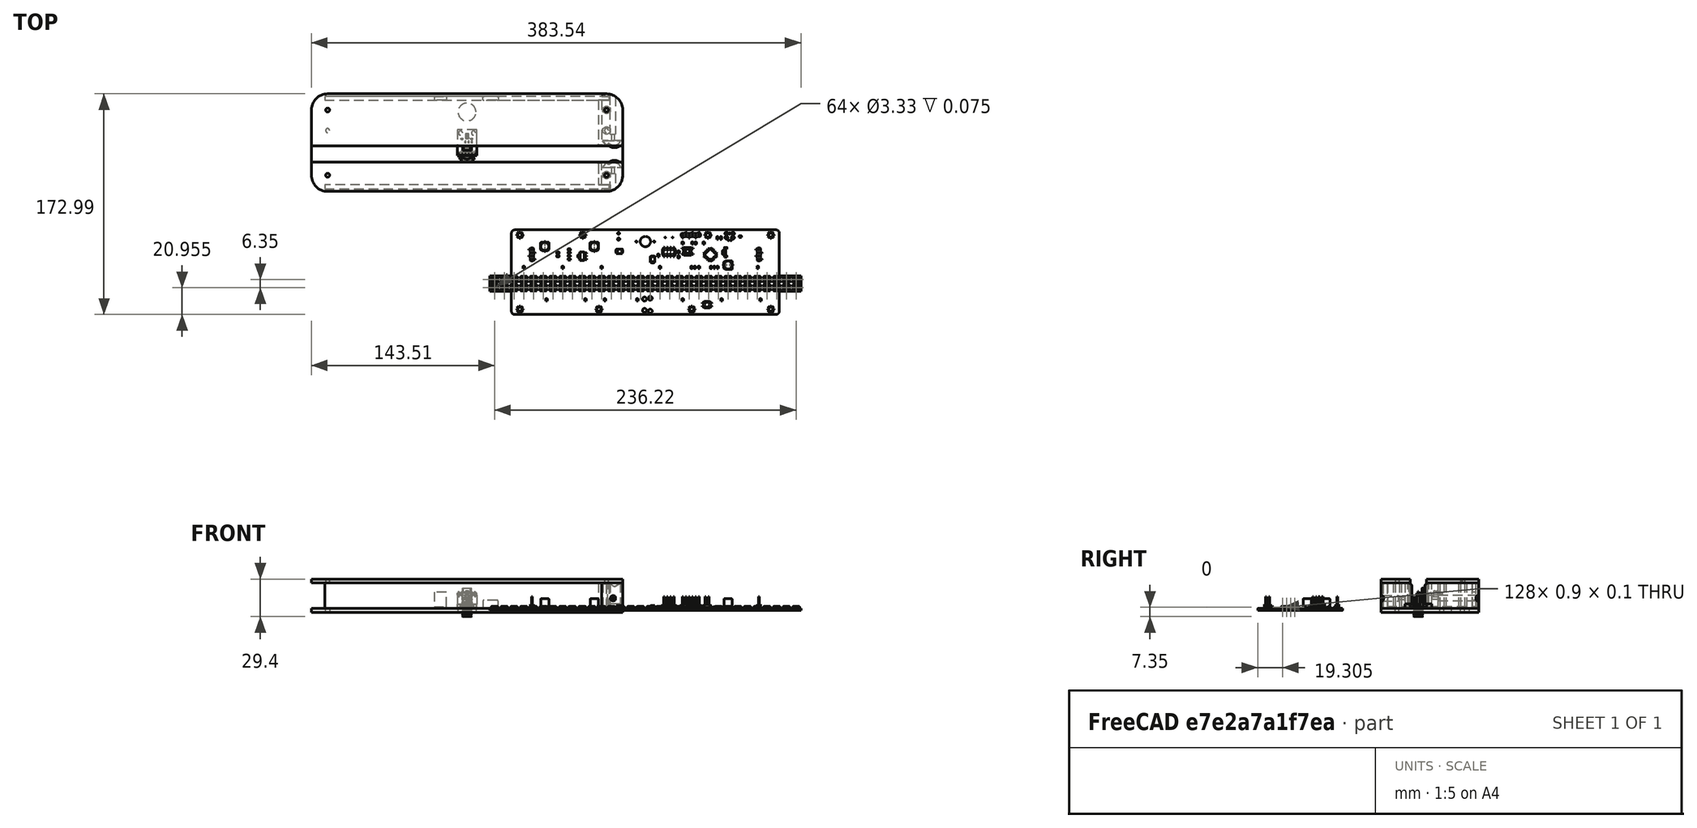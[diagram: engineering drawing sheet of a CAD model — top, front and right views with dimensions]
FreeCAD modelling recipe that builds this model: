
FCSTD DOCUMENT  (FreeCAD 0.21R33675 (Git))
Label: mockup_v2
License: All rights reserved
LicenseURL: http://en.wikipedia.org/wiki/All_rights_reserved
objects: Part::Feature×143, Sketcher::SketchObject×30, PartDesign::Pocket×15, PartDesign::Pad×13, PartDesign::Body×9, App::Part×8, PartDesign::SubShapeBinder×7, Part::Part2DObjectPython×6, PartDesign::ShapeBinder×3, PartDesign::Plane×3, TechDraw::DrawViewDimension×3, Part::Mirroring×2, PartDesign::CoordinateSystem×1, PartDesign::Mirrored×1, Part::FeaturePython×1, TechDraw::DrawSVGTemplate×1, TechDraw::DrawViewPart×1, TechDraw::DrawHatch×1, TechDraw::DrawPage×1
note: 262 computed .brp shape members not serialized (recipe doc carries the construction recipe); baked Part::Feature solids carry a one-line shape summary decoded from their .brp

FEATURE [Sketcher::SketchObject] Sketch
  FullyConstrained = true
  MapMode = 5
  Support = -> [XY_Plane]
  expr: Constraints[14] = 96.52 mm - 20 mm
  expr: Constraints[29] = 17.1 mm - 1 mm
  expr: Constraints[30] = 48.26 mm - 1 mm
  sketch-geometry (15):
    g0: LineSegment StartX=-109.22 StartY=47.26 StartZ=0 EndX=109.22 EndY=47.26 EndZ=0
    g1: LineSegment StartX=121.92 StartY=34.56 StartZ=0 EndX=121.92 EndY=-16.56 EndZ=0
    g2: LineSegment StartX=109.22 StartY=-29.26 StartZ=0 EndX=-109.22 EndY=-29.26 EndZ=0
    g3: LineSegment StartX=-121.92 StartY=-16.56 StartZ=0 EndX=-121.92 EndY=34.56 EndZ=0
    g4: ArcOfCircle CenterX=-109.22 CenterY=34.56 CenterZ=0 NormalX=0 NormalY=0 NormalZ=1 AngleXU=0 Radius=12.7 StartAngle=1.5708 EndAngle=3.14159
    g5: ArcOfCircle CenterX=-109.22 CenterY=-16.56 CenterZ=0 NormalX=0 NormalY=0 NormalZ=1 AngleXU=0 Radius=12.7 StartAngle=3.14159 EndAngle=4.71239
    g6: ArcOfCircle CenterX=109.22 CenterY=-16.56 CenterZ=0 NormalX=0 NormalY=0 NormalZ=1 AngleXU=0 Radius=12.7 StartAngle=4.71239 EndAngle=6.28319
    g7: ArcOfCircle CenterX=109.22 CenterY=34.56 CenterZ=0 NormalX=0 NormalY=0 NormalZ=1 AngleXU=0 Radius=12.7 StartAngle=-1.17497e-11 EndAngle=1.5708
    g8: Circle CenterX=-109.22 CenterY=34.56 CenterZ=0 NormalX=0 NormalY=0 NormalZ=1 AngleXU=0 Radius=1.55
    g9: Circle CenterX=-109.22 CenterY=-16.56 CenterZ=0 NormalX=0 NormalY=0 NormalZ=1 AngleXU=0 Radius=1.55
    g10: Circle CenterX=109.22 CenterY=34.56 CenterZ=0 NormalX=0 NormalY=0 NormalZ=1 AngleXU=0 Radius=1.55
    g11: Circle CenterX=109.22 CenterY=-16.56 CenterZ=0 NormalX=0 NormalY=0 NormalZ=1 AngleXU=0 Radius=1.55
    g12: Circle CenterX=-109.22 CenterY=18.46 CenterZ=0 NormalX=0 NormalY=0 NormalZ=1 AngleXU=0 Radius=1.55
    g13: Circle CenterX=109.22 CenterY=18.46 CenterZ=0 NormalX=0 NormalY=0 NormalZ=1 AngleXU=0 Radius=1.55
    g14: Circle CenterX=0 CenterY=33.02 CenterZ=0 NormalX=0 NormalY=0 NormalZ=1 AngleXU=0 Radius=7
  constraints (36):
    c: Horizontal(g0)
    c: Horizontal(g2)
    c: Vertical(g1)
    c: Vertical(g3)
    c: Tangent(g0,g4) = 1.5708
    c: Tangent(g3,g4) = 1.5708
    c: Tangent(g3,g5) = 1.5708
    c: Tangent(g2,g5) = 1.5708
    c: Tangent(g2,g6) = 1.5708
    c: Tangent(g1,g6) = 1.5708
    c: Tangent(g1,g7) = 1.5708
    c: Tangent(g0,g7) = 1.5708
    c: Equal(g5,g6)
    c: DistanceX(g3,g1) = 243.84
    c: DistanceY(g2,g0) = 76.52
    c: Radius(g4) = 12.7
    c: Symmetric(g3,g1,g-2)
    c: Coincident(g8,g4)
    c: Coincident(g9,g5)
    c: Coincident(g10,g7)
    c: Coincident(g11,g6)
    c: Radius(g9) = 1.55
    c: Equal(g9,g8)
    c: Equal(g9,g10)
    c: Equal(g9,g11)
    c: Equal(g13,g12)
    c: DistanceX(g4,g12) = 0
    c: DistanceY(g12,g4) = 16.1
    c: DistanceX(g7,g13) = 0
    c: DistanceY(g13,g7) = 16.1
    c: DistanceY(g-1,g0) = 47.26
    c: Equal(g5,g4)
    c: Equal(g13,g10)
    c: PointOnObject(g14,g-2)
    c: Radius(g14) = 7
    c: DistanceY(g-1,g14) = 33.02
FEATURE [PartDesign::Pad] Pad
  Direction = (1,1,1)
  Length = 3
  Length2 = 100
  Profile = -> Sketch
  Reversed = true
  Type = 0
FEATURE [PartDesign::Body] Body  label="ACR_bottom"
  Group = -> [Sketch,Pad]
  Origin = -> Origin
  Tip = -> Pad
FEATURE [Sketcher::SketchObject] Sketch001
  AttachmentOffset = pos=(0,0,1.6) rot=(0,0,1;0rad)
  FullyConstrained = true
  MapMode = 5
  Placement = pos=(0,0,1.6) rot=(0,0,1;0rad)
  Support = -> [XY_Plane001]
  sketch-geometry (4):
    g0: LineSegment StartX=-127 StartY=6 StartZ=0 EndX=127 EndY=6 EndZ=0
    g1: LineSegment StartX=127 StartY=6 StartZ=0 EndX=127 EndY=0 EndZ=0
    g2: LineSegment StartX=127 StartY=0 StartZ=0 EndX=-127 EndY=0 EndZ=0
    g3: LineSegment StartX=-127 StartY=0 StartZ=0 EndX=-127 EndY=6 EndZ=0
  constraints (11):
    c: Coincident(g0,g1)
    c: Coincident(g1,g2)
    c: Coincident(g2,g3)
    c: Coincident(g3,g0)
    c: Horizontal(g0)
    c: Vertical(g1)
    c: Vertical(g3)
    c: Symmetric(g2,g1,g-2)
    c: DistanceY(g1,g1) = 6
    c: DistanceX(g0,g0) = 254
    c: PointOnObject(g-1,g2)
FEATURE [PartDesign::Pad] Pad001
  Direction = (1,1,1)
  Length = 254
  Length2 = 100
  Profile = -> Sketch001
  Type = 0
FEATURE [PartDesign::Body] Body001  label="ACR_back"
  Group = -> [Sketch001,Pad001]
  Origin = -> Origin001
  Placement = pos=(0,0,1.6) rot=(0,0,1;0rad)
  Tip = -> Pad001
FEATURE [Sketcher::SketchObject] Sketch002
  AttachmentOffset = pos=(0,0,1.6) rot=(0,0,1;0rad)
  FullyConstrained = true
  MapMode = 5
  Placement = pos=(0,0,1.6) rot=(0,0,1;0rad)
  Support = -> [XY_Plane002]
  sketch-geometry (4):
    g0: LineSegment StartX=-127 StartY=6 StartZ=0 EndX=127 EndY=6 EndZ=0
    g1: LineSegment StartX=127 StartY=6 StartZ=0 EndX=127 EndY=0 EndZ=0
    g2: LineSegment StartX=127 StartY=0 StartZ=0 EndX=-127 EndY=0 EndZ=0
    g3: LineSegment StartX=-127 StartY=0 StartZ=0 EndX=-127 EndY=6 EndZ=0
  constraints (11):
    c: Coincident(g0,g1)
    c: Coincident(g1,g2)
    c: Coincident(g2,g3)
    c: Coincident(g3,g0)
    c: Horizontal(g0)
    c: Vertical(g1)
    c: Vertical(g3)
    c: Symmetric(g2,g1,g-2)
    c: DistanceY(g1,g1) = 6
    c: DistanceX(g0,g0) = 254
    c: PointOnObject(g-1,g2)
FEATURE [PartDesign::Pad] Pad002
  Direction = (1,1,1)
  Length = 254
  Length2 = 100
  Profile = -> Sketch002
  Type = 0
FEATURE [PartDesign::ShapeBinder] ShapeBinder004
  Placement = pos=(0,0,20) rot=(0,0,1;0rad)
  TraceSupport = false
FEATURE [PartDesign::ShapeBinder] ShapeBinder005
  Placement = pos=(0,0,20) rot=(0,0,1;0rad)
  TraceSupport = false
FEATURE [Sketcher::SketchObject] Sketch006
  ExternalGeometry = -> [ShapeBinder005,ShapeBinder004]
  FullyConstrained = true
  MapMode = 5
  Support = -> [XY_Plane006]
  sketch-geometry (8):
    g0: LineSegment StartX=-111.5 StartY=-46.1898 StartZ=0 EndX=111.5 EndY=-46.1898 EndZ=0
    g1: LineSegment StartX=111.5 StartY=-46.1898 StartZ=0 EndX=111.5 EndY=-43.1898 EndZ=0
    g2: LineSegment StartX=111.5 StartY=-43.1898 StartZ=0 EndX=-111.5 EndY=-43.1898 EndZ=0
    g3: LineSegment StartX=-111.5 StartY=-43.1898 StartZ=0 EndX=-111.5 EndY=-46.1898 EndZ=0
    g4: LineSegment StartX=111.5 StartY=-43.1898 StartZ=0 EndX=111.8 EndY=-43.1398 EndZ=0
    g5: LineSegment StartX=111.5 StartY=-46.1898 StartZ=0 EndX=111.8 EndY=-46.2398 EndZ=0
    g6: LineSegment StartX=-111.5 StartY=-46.1898 StartZ=0 EndX=-111.8 EndY=-46.2398 EndZ=0
    g7: LineSegment StartX=-111.5 StartY=-43.1898 StartZ=0 EndX=-111.8 EndY=-43.1398 EndZ=0
  constraints (20):
    c: Coincident(g0,g1)
    c: Coincident(g1,g2)
    c: Coincident(g2,g3)
    c: Coincident(g3,g0)
    c: Horizontal(g0)
    c: Horizontal(g2)
    c: Vertical(g1)
    c: Coincident(g4,g1)
    c: Coincident(g4,g-4)
    c: Coincident(g5,g0)
    c: Coincident(g5,g-4)
    c: Coincident(g6,g0)
    c: Coincident(g6,g-3)
    c: Coincident(g7,g2)
    c: Coincident(g7,g-3)
    c: Equal(g6,g7)
    c: Equal(g7,g4)
    c: Equal(g4,g5)
    c: DistanceY(g1,g1) = 3
    c: DistanceX(g0,g0) = 223
FEATURE [PartDesign::Pad] Pad006
  Direction = (1,1,1)
  Length = 20
  Length2 = 100
  Profile = -> Sketch006
  Type = 0
FEATURE [PartDesign::Body] Body006  label="ACR_wall_front"
  Group = -> [Sketch006,ShapeBinder004,ShapeBinder005,Pad006]
  Origin = -> Origin006
  Placement = pos=(0,19,0) rot=(0,0,1;0rad)
  Tip = -> Pad006
FEATURE [Sketcher::SketchObject] Sketch016
  FullyConstrained = true
  MapMode = 5
  sketch-geometry (12):
    g0: ArcOfCircle CenterX=-109.22 CenterY=-35.56 CenterZ=0 NormalX=0 NormalY=0 NormalZ=1 AngleXU=0 Radius=12.7 StartAngle=3.14159 EndAngle=5.01213
    g1: LineSegment StartX=-105.47 StartY=-43.1237 StartZ=0 EndX=-111.97 EndY=-43.1237 EndZ=0
    g2: LineSegment StartX=-111.97 StartY=-43.1237 StartZ=0 EndX=-111.97 EndY=-46.2237 EndZ=0
    g3: LineSegment StartX=-111.97 StartY=-46.2237 StartZ=0 EndX=-105.47 EndY=-46.2237 EndZ=0
    g4: LineSegment StartX=-105.47 StartY=-46.2237 StartZ=0 EndX=-105.47 EndY=-47.6937 EndZ=0
    g5: LineSegment StartX=-105.47 StartY=-31.6937 StartZ=0 EndX=-105.47 EndY=-43.1237 EndZ=0
    g6: Circle CenterX=-109.22 CenterY=-35.56 CenterZ=0 NormalX=0 NormalY=0 NormalZ=1 AngleXU=0 Radius=2.4
    g7: LineSegment StartX=-105.47 StartY=-31.6937 StartZ=0 EndX=-105.47 EndY=-26.1937 EndZ=0
    g8: ArcOfCircle CenterX=-106.27 CenterY=-26.1937 CenterZ=0 NormalX=0 NormalY=0 NormalZ=1 AngleXU=0 Radius=0.8 StartAngle=-1.8e-15 EndAngle=1.44549
    g9: LineSegment StartX=-106.17 StartY=-25.4 StartZ=0 EndX=-121.92 EndY=-25.4 EndZ=0
    g10: LineSegment StartX=-121.92 StartY=-25.4 StartZ=0 EndX=-121.92 EndY=-35.56 EndZ=0
    g11: LineSegment StartX=-109.22 StartY=-35.56 StartZ=0 EndX=-121.92 EndY=-35.56 EndZ=0
  constraints (35):
    c: Coincident(g0,g4)
    c: Coincident(g1,g2)
    c: Coincident(g2,g3)
    c: Horizontal(g1)
    c: Horizontal(g3)
    c: Vertical(g2)
    c: DistanceY(g2,g2) = 3.1
    c: Coincident(g4,g3)
    c: DistanceY(g0,g5) = 16
    c: Coincident(g5,g1)
    c: Vertical(g5)
    c: DistanceY(g1,g5) = 11.43
    c: Vertical(g4)
    c: Equal(g1,g3)
    c: Coincident(g6,g0)
    c: Radius(g6) = 2.4
    c: Vertical(g7)
    c: Tangent(g7,g8) = -1.5708
    c: Coincident(g8,g9)
    c: Horizontal(g9)
    c: Coincident(g9,g10)
    c: Vertical(g10)
    c: Coincident(g0,g10)
    c: DistanceY(g7,g7) = 5.5
    c: Radius(g8) = 0.8
    c: DistanceX(g9,g9) = 15.75
    c: DistanceY(g10,g10) = 10.16
    c: Coincident(g11,g0)
    c: Coincident(g11,g0)
    c: Horizontal(g11)
    c: DistanceX(g-2,g0) = -109.22
    c: DistanceY(g-1,g0) = -35.56
    c: DistanceX(g1,g1) = 6.5
    c: Radius(g0) = 12.7
    c: Coincident(g5,g7)
FEATURE [PartDesign::Pad] Pad017
  Direction = (1,1,1)
  Length = 20
  Length2 = 100
  Profile = -> Sketch016
  Type = 0
FEATURE [Sketcher::SketchObject] Sketch020
  ExternalGeometry = -> [Pad017]
  FullyConstrained = true
  MapMode = 5
  Placement = pos=(0,0,20) rot=(0,0,1;0rad)
  Support = -> [Pad017]
  sketch-geometry (4):
    g0: LineSegment StartX=-105.47 StartY=-26.1937 StartZ=0 EndX=-102.97 EndY=-26.1937 EndZ=0
    g1: LineSegment StartX=-102.97 StartY=-26.1937 StartZ=0 EndX=-102.97 EndY=-43.1237 EndZ=0
    g2: LineSegment StartX=-102.97 StartY=-43.1237 StartZ=0 EndX=-105.47 EndY=-43.1237 EndZ=0
    g3: LineSegment StartX=-105.47 StartY=-43.1237 StartZ=0 EndX=-105.47 EndY=-26.1937 EndZ=0
  constraints (10):
    c: Coincident(g0,g1)
    c: Coincident(g1,g2)
    c: Coincident(g2,g3)
    c: Coincident(g3,g0)
    c: Horizontal(g0)
    c: Horizontal(g2)
    c: Vertical(g1)
    c: DistanceX(g0,g0) = 2.5
    c: Coincident(g0,g-3)
    c: Coincident(g2,g-4)
FEATURE [PartDesign::Pad] Pad021
  BaseFeature = -> Pad017
  Direction = (1,1,1)
  Length = 18.3
  Length2 = 100
  Profile = -> Sketch020
  Refine = true
  Reversed = true
  Type = 0
FEATURE [PartDesign::CoordinateSystem] Local_CS_a344
  AttacherType = Attacher::AttachEngine3D
FEATURE [Part::Feature] Pcb_a344
  shape: bbox 243.8 x 66.29 x 1.6 mm, 114 faces (baked)
FEATURE [Sketcher::SketchObject] PCB_Sketch_a344
  FullyConstrained = false
  sketch-geometry (22):
    g0: LineSegment StartX=37.338 StartY=-125.73 StartZ=0 EndX=139.7 EndY=-125.73 EndZ=0
    g1: LineSegment StartX=34.798 StartY=-108.966 StartZ=0 EndX=34.798 EndY=-123.19 EndZ=0
    g2: LineSegment StartX=17.78 StartY=-107.696 StartZ=0 EndX=33.528 EndY=-107.696 EndZ=0
    g3: LineSegment StartX=17.78 StartY=-107.696 StartZ=0 EndX=17.78 EndY=-95.504 EndZ=0
    g4: LineSegment StartX=17.78 StartY=-95.504 StartZ=0 EndX=33.528 EndY=-95.504 EndZ=0
    g5: LineSegment StartX=34.798 StartY=-94.234 StartZ=0 EndX=34.798 EndY=-61.976 EndZ=0
    g6: LineSegment StartX=139.7 StartY=-59.436 StartZ=0 EndX=242.062 EndY=-59.436 EndZ=0
    g7: LineSegment StartX=244.602 StartY=-94.234 StartZ=0 EndX=244.602 EndY=-61.976 EndZ=0
    g8: LineSegment StartX=245.872 StartY=-95.504 StartZ=0 EndX=261.62 EndY=-95.504 EndZ=0
    g9: LineSegment StartX=261.62 StartY=-107.696 StartZ=0 EndX=261.62 EndY=-95.504 EndZ=0
    g10: LineSegment StartX=245.872 StartY=-107.696 StartZ=0 EndX=261.62 EndY=-107.696 EndZ=0
    g11: LineSegment StartX=244.602 StartY=-108.966 StartZ=0 EndX=244.602 EndY=-123.19 EndZ=0
    g12: LineSegment StartX=139.7 StartY=-125.73 StartZ=0 EndX=242.062 EndY=-125.73 EndZ=0
    g13: LineSegment StartX=37.338 StartY=-59.436 StartZ=0 EndX=139.7 EndY=-59.436 EndZ=0
    g14: ArcOfCircle CenterX=242.062 CenterY=-123.19 CenterZ=0 NormalX=0 NormalY=0 NormalZ=1 AngleXU=0 Radius=2.54 StartAngle=4.71239 EndAngle=6.28319
    g15: ArcOfCircle CenterX=242.062 CenterY=-61.976 CenterZ=0 NormalX=0 NormalY=0 NormalZ=1 AngleXU=0 Radius=2.54 StartAngle=0 EndAngle=1.5708
    g16: ArcOfCircle CenterX=37.338 CenterY=-123.19 CenterZ=0 NormalX=0 NormalY=0 NormalZ=1 AngleXU=0 Radius=2.54 StartAngle=3.14159 EndAngle=4.71239
    g17: ArcOfCircle CenterX=37.338 CenterY=-61.976 CenterZ=0 NormalX=0 NormalY=0 NormalZ=1 AngleXU=0 Radius=2.54 StartAngle=1.5708 EndAngle=3.14159
    g18: ArcOfCircle CenterX=245.872 CenterY=-108.966 CenterZ=0 NormalX=0 NormalY=0 NormalZ=1 AngleXU=0 Radius=1.27 StartAngle=1.5708 EndAngle=3.14159
    g19: ArcOfCircle CenterX=245.872 CenterY=-94.234 CenterZ=0 NormalX=0 NormalY=0 NormalZ=1 AngleXU=0 Radius=1.27 StartAngle=3.14159 EndAngle=4.71239
    g20: ArcOfCircle CenterX=33.528 CenterY=-108.966 CenterZ=0 NormalX=0 NormalY=0 NormalZ=1 AngleXU=0 Radius=1.27 StartAngle=0 EndAngle=1.5708
    g21: ArcOfCircle CenterX=33.528 CenterY=-94.234 CenterZ=0 NormalX=0 NormalY=0 NormalZ=1 AngleXU=0 Radius=1.27 StartAngle=4.71239 EndAngle=6.28319
  constraints (22):
    c: Coincident(g2,g3)
    c: Coincident(g3,g4)
    c: Coincident(g20,g2)
    c: Coincident(g21,g4)
    c: Coincident(g16,g1)
    c: Coincident(g1,g20)
    c: Coincident(g5,g21)
    c: Coincident(g5,g17)
    c: Coincident(g0,g16)
    c: Coincident(g17,g13)
    c: Coincident(g0,g12)
    c: Coincident(g6,g13)
    c: Coincident(g12,g14)
    c: Coincident(g6,g15)
    c: Coincident(g11,g14)
    c: Coincident(g18,g11)
    c: Coincident(g19,g7)
    c: Coincident(g15,g7)
    c: Coincident(g10,g18)
    c: Coincident(g8,g19)
    c: Coincident(g9,g10)
    c: Coincident(g9,g8)
FEATURE [App::Part] Board_Geoms_a344
  Group = -> [Local_CS_a344,Pcb_a344,PCB_Sketch_a344]
  Origin = -> Origin148
FEATURE [Part::Feature] Shape  label="C17_C_0805_2012Metric_5FD6B1FA"
  Placement = pos=(149.86,-79.4512,0) rot=(0,0,1;1.5708rad)
  shape: bbox 1.25 x 2 x 1.25 mm, 28 faces (baked)
FEATURE [Part::Feature] Part__Feature  label="barrel_jack_DC_005_5A_2_5_SMT"
  shape: bbox 1.5 x 1.8 x 0.9949 mm, 1656 faces, 0 solids (baked)
FEATURE [Part::Feature] Part__Feature001  label="barrel_jack_DC_005_5A_2_5_SMT001"
  shape: bbox 1.5 x 1.8 x 2.5 mm, 1382 faces, 0 solids (baked)
FEATURE [Part::Feature] Part__Feature002  label="barrel_jack_DC_005_5A_2_5_SMT002"
  shape: bbox 14.8 x 10.8 x 12.4 mm, 11202 faces, 0 solids (baked)
FEATURE [App::Part] barrel_jack_DC_005_5A_2_5_SMT  label="J3_barrel_jack_DC_005_5A_2_5_SMT003_5FD6A57F"
  Group = -> [Part__Feature,Part__Feature001,Part__Feature002]
  Origin = -> Origin156
  Placement = pos=(118.745,-57.15,0) rot=(0,0,-1;1.5708rad)
FEATURE [Part::Feature] Part__Feature003  label="sparkfun_apds_9960"
  shape: bbox 15.24 x 21.55 x 16.01 mm, 533 faces (baked)
FEATURE [Part::Feature] Part__Feature004  label="sparkfun_apds_9961"
  shape: bbox 2.36 x 1.15 x 1.1 mm, 21 faces (baked)
FEATURE [Part::Feature] Part__Feature005  label="sparkfun_apds_9962"
  shape: bbox 2.36 x 3.835 x 1.35 mm, 67 faces (baked)
FEATURE [App::Part] sparkfun_apds_9960  label="P5_sparkfun_apds_9963_5FD6A7AB"
  Group = -> [Part__Feature003,Part__Feature004,Part__Feature005]
  Origin = -> Origin157
  Placement = pos=(127,-118.11,0) rot=(0,0,-1;1.5708rad)
FEATURE [Part::Feature] Part__Feature006  label="USB4110_GF_A018_cp"
  shape: bbox 0.2 x 0.6 x 0.15 mm, 6 faces (baked)
FEATURE [Part::Feature] Part__Feature007  label="USB4110_GF_A018_cp001"
  shape: bbox 0.2 x 0.6 x 0.15 mm, 6 faces (baked)
FEATURE [Part::Feature] Part__Feature008  label="USB4110_GF_A018_cp002"
  shape: bbox 0.2 x 0.6 x 0.15 mm, 6 faces (baked)
FEATURE [Part::Feature] Part__Feature009  label="USB4110_GF_A018_cp003"
  shape: bbox 0.2 x 0.6 x 0.15 mm, 6 faces (baked)
FEATURE [Part::Feature] Part__Feature010  label="USB4110_GF_A018_cp004"
  shape: bbox 0.2 x 0.6 x 0.15 mm, 6 faces (baked)
FEATURE [Part::Feature] Part__Feature011  label="USB4110_GF_A018_cp005"
  shape: bbox 0.2 x 0.6 x 0.15 mm, 6 faces (baked)
FEATURE [Part::Feature] Part__Feature012  label="USB4110_GF_A018_cp006"
  shape: bbox 0.2 x 0.6 x 0.15 mm, 6 faces (baked)
FEATURE [Part::Feature] Part__Feature013  label="USB4110_GF_A018_cp007"
  shape: bbox 0.2 x 0.6 x 0.15 mm, 6 faces (baked)
FEATURE [Part::Feature] Part__Feature014  label="USB4110_GF_A018_cp008"
  shape: bbox 0.2 x 0.6 x 0.15 mm, 6 faces (baked)
FEATURE [Part::Feature] Part__Feature015  label="USB4110_GF_A018_cp009"
  shape: bbox 0.2 x 0.6 x 0.15 mm, 6 faces (baked)
FEATURE [Part::Feature] Part__Feature016  label="USB4110_GF_A018_cp010"
  shape: bbox 0.2 x 0.6 x 0.15 mm, 6 faces (baked)
FEATURE [Part::Feature] Part__Feature017  label="USB4110_GF_A018_cp011"
  shape: bbox 0.2 x 0.6 x 0.15 mm, 6 faces (baked)
FEATURE [Part::Feature] Part__Feature018  label="USB4110_GF_A018_cp012"
  shape: bbox 0.2 x 0.6 x 0.15 mm, 6 faces (baked)
FEATURE [Part::Feature] Part__Feature019  label="USB4110_GF_A018_cp013"
  shape: bbox 0.2 x 0.6 x 0.15 mm, 6 faces (baked)
FEATURE [Part::Feature] Part__Feature020  label="USB4110_GF_A018_cp014"
  shape: bbox 0.2 x 0.6 x 0.15 mm, 6 faces (baked)
FEATURE [Part::Feature] Part__Feature021  label="USB4110_GF_A018_cp015"
  shape: bbox 0.2 x 0.6 x 0.15 mm, 6 faces (baked)
FEATURE [Part::Feature] Part__Feature022  label="USB4110_GF_A018_cp016"
  shape: bbox 8.94 x 7.05 x 3.66 mm, 301 faces (baked)
FEATURE [Part::Feature] Part__Feature023  label="USB4110_GF_A018_cp017"
  shape: bbox 11.31 x 7.338 x 3.268 mm, 337 faces (baked)
FEATURE [App::Part] USB4110_GF_A018_cp  label="J2_USB4110_GF_A018_cp018_5FD6A740"
  Group = -> [Part__Feature006,Part__Feature007,Part__Feature008,Part__Feature009,Part__Feature010,Part__Feature011,Part__Feature012,Part__Feature013,Part__Feature014,Part__Feature015,Part__Feature016,Part__Feature017,Part__Feature018,Part__Feature019,Part__Feature020,Part__Feature021,Part__Feature022,Part__Feature023]
  Origin = -> Origin158
  Placement = pos=(158.115,-65.405,0) rot=(0,0,1;3.14159rad)
FEATURE [Part::Feature] Shape001  label="C20_C_0805_2012Metric_5FD69613"
  Placement = pos=(176.53,-69.85,0) rot=(0,0,-1;1.5708rad)
  shape: bbox 1.25 x 2 x 1.25 mm, 28 faces (baked)
FEATURE [Part::Feature] Shape002  label="U2_SOT_223_5FD6A8DB"
  Placement = pos=(90.17,-80.01,0) rot=(0,0,1;3.14159rad)
  shape: bbox 7 x 6.5 x 1.7 mm, 78 faces (baked)
FEATURE [Part::Feature] Shape003  label="R8_R_0805_2012Metric_5FD6A3A8"
  Placement = pos=(198.882,-65.786,0) rot=(0,0,1;1.5708rad)
  shape: bbox 1.2 x 2 x 0.45 mm, 26 faces (baked)
FEATURE [Part::Feature] Shape004  label="D2_LED_WS2812B_PLCC4_50x50mm_P32mm_5FD31A96"
  Placement = pos=(21.59,-104.775,0) rot=(0,0,1;0rad)
  shape: bbox 5.4 x 5 x 1.6 mm, 68 faces (baked)
FEATURE [Part::Feature] Shape005  label="D33_D_SMB_5FD6A65A"
  Placement = pos=(145.415,-82.55,0) rot=(0,0,1;1.5708rad)
  shape: bbox 3.55 x 5.3 x 2.15 mm, 41 faces (baked)
FEATURE [Part::Feature] Shape006  label="C11_C_0805_2012Metric_5FD6947B"
  Placement = pos=(44.45,-88.9,0) rot=(0,0,-1;1.5708rad)
  shape: bbox 1.25 x 2 x 1.25 mm, 28 faces (baked)
FEATURE [Part::Feature] Shape007  label="C18_C_0805_2012Metric_5FD69166"
  Placement = pos=(133.35,-114.3,0) rot=(0,0,1;1.5708rad)
  shape: bbox 1.25 x 2 x 1.25 mm, 28 faces (baked)
FEATURE [Part::Feature] Shape008  label="C10_C_0805_2012Metric_5FD6A378"
  Placement = pos=(213.995,-64.77,0) rot=(0,0,1;3.14159rad)
  shape: bbox 2 x 1.25 x 1.25 mm, 28 faces (baked)
FEATURE [Part::Feature] Shape009  label="C6_C_0805_2012Metric_5FD6ACED"
  Placement = pos=(202.565,-73.787,0) rot=(0,0,1;3.14159rad)
  shape: bbox 2 x 1.25 x 1.25 mm, 28 faces (baked)
FEATURE [Part::Feature] Shape010  label="C9_C_0805_2012Metric_5FD6AED3"
  Placement = pos=(168.91,-69.85,0) rot=(0,0,-1;1.5708rad)
  shape: bbox 1.25 x 2 x 1.25 mm, 28 faces (baked)
FEATURE [Part::Feature] Shape011  label="R1_R_0805_2012Metric_5FD694C9"
  Placement = pos=(179.07,-69.85,0) rot=(0,0,-1;1.5708rad)
  shape: bbox 1.2 x 2 x 0.45 mm, 26 faces (baked)
FEATURE [Part::Feature] Shape012  label="C2_C_0805_2012Metric_5FD69643"
  Placement = pos=(185.42,-69.85,0) rot=(0,0,1;1.5708rad)
  shape: bbox 1.25 x 2 x 1.25 mm, 28 faces (baked)
FEATURE [Part::Feature] Shape013  label="C3_C_0805_2012Metric_5FD6B0EC"
  Placement = pos=(196.215,-88.9,0) rot=(0,0,-1;1.5708rad)
  shape: bbox 1.25 x 2 x 1.25 mm, 28 faces (baked)
FEATURE [Part::Feature] Shape014  label="C4_C_0805_2012Metric_5FD695B0"
  Placement = pos=(193.675,-88.9,0) rot=(0,0,-1;1.5708rad)
  shape: bbox 1.25 x 2 x 1.25 mm, 28 faces (baked)
FEATURE [Part::Feature] Shape015  label="C5_C_0805_2012Metric_5FD6A6FC"
  Placement = pos=(202.565,-80.264,0) rot=(0,0,1;0rad)
  shape: bbox 2 x 1.25 x 1.25 mm, 28 faces (baked)
FEATURE [Part::Feature] Shape016  label="C8_C_0805_2012Metric_5FD69199"
  Placement = pos=(80.01,-80.01,0) rot=(0,0,1;3.14159rad)
  shape: bbox 2 x 1.25 x 1.25 mm, 28 faces (baked)
FEATURE [Part::Feature] Shape017  label="D3_LED_WS2812B_PLCC4_50x50mm_P32mm_5FA1A33E"
  Placement = pos=(29.21,-104.775,0) rot=(0,0,1;3.14159rad)
  shape: bbox 5.4 x 5 x 1.6 mm, 68 faces (baked)
FEATURE [Part::Feature] Shape018  label="D4_LED_WS2812B_PLCC4_50x50mm_P32mm_5FA1AF0B"
  Placement = pos=(29.21,-98.425,0) rot=(0,0,1;3.14159rad)
  shape: bbox 5.4 x 5 x 1.6 mm, 68 faces (baked)
FEATURE [Part::Feature] Shape019  label="D10_LED_WS2812B_PLCC4_50x50mm_P32mm_5FA1A6EF"
  Placement = pos=(52.07,-104.775,0) rot=(0,0,1;0rad)
  shape: bbox 5.4 x 5 x 1.6 mm, 68 faces (baked)
FEATURE [Part::Feature] Shape020  label="D11_LED_WS2812B_PLCC4_50x50mm_P32mm_5FA1BA8A"
  Placement = pos=(59.69,-104.775,0) rot=(0,0,1;3.14159rad)
  shape: bbox 5.4 x 5 x 1.6 mm, 68 faces (baked)
FEATURE [Part::Feature] Shape021  label="D17_LED_WS2812B_PLCC4_50x50mm_P32mm_5FA1BB86"
  Placement = pos=(82.55,-98.425,0) rot=(0,0,1;0rad)
  shape: bbox 5.4 x 5 x 1.6 mm, 68 faces (baked)
FEATURE [Part::Feature] Shape022  label="D18_LED_WS2812B_PLCC4_50x50mm_P32mm_5FA1B54A"
  Placement = pos=(82.55,-104.775,0) rot=(0,0,1;0rad)
  shape: bbox 5.4 x 5 x 1.6 mm, 68 faces (baked)
FEATURE [Part::Feature] Shape023  label="D19_LED_WS2812B_PLCC4_50x50mm_P32mm_5FD0FC67"
  Placement = pos=(90.17,-104.775,0) rot=(0,0,1;3.14159rad)
  shape: bbox 5.4 x 5 x 1.6 mm, 68 faces (baked)
FEATURE [Part::Feature] Shape024  label="D20_LED_WS2812B_PLCC4_50x50mm_P32mm_5FA1AE42"
  Placement = pos=(90.17,-98.425,0) rot=(0,0,1;3.14159rad)
  shape: bbox 5.4 x 5 x 1.6 mm, 68 faces (baked)
FEATURE [Part::Feature] Shape025  label="D21_LED_WS2812B_PLCC4_50x50mm_P32mm_5FA1B03D"
  Placement = pos=(97.79,-98.425,0) rot=(0,0,1;0rad)
  shape: bbox 5.4 x 5 x 1.6 mm, 68 faces (baked)
FEATURE [Part::Feature] Shape026  label="D22_LED_WS2812B_PLCC4_50x50mm_P32mm_5FA1ADFD"
  Placement = pos=(97.79,-104.775,0) rot=(0,0,1;0rad)
  shape: bbox 5.4 x 5 x 1.6 mm, 68 faces (baked)
FEATURE [Part::Feature] Shape027  label="D23_LED_WS2812B_PLCC4_50x50mm_P32mm_5FA1B26B"
  Placement = pos=(105.41,-104.775,0) rot=(0,0,1;3.14159rad)
  shape: bbox 5.4 x 5 x 1.6 mm, 68 faces (baked)
FEATURE [Part::Feature] Shape028  label="D28_LED_WS2812B_PLCC4_50x50mm_P32mm_5FD3357B"
  Placement = pos=(120.65,-98.425,0) rot=(0,0,1;3.14159rad)
  shape: bbox 5.4 x 5 x 1.6 mm, 68 faces (baked)
FEATURE [Part::Feature] Shape029  label="D29_LED_WS2812B_PLCC4_50x50mm_P32mm_5FD10914"
  Placement = pos=(128.27,-98.425,0) rot=(0,0,1;0rad)
  shape: bbox 5.4 x 5 x 1.6 mm, 68 faces (baked)
FEATURE [Part::Feature] Shape030  label="D30_LED_WS2812B_PLCC4_50x50mm_P32mm_5FA1AA61"
  Placement = pos=(128.27,-104.775,0) rot=(0,0,1;0rad)
  shape: bbox 5.4 x 5 x 1.6 mm, 68 faces (baked)
FEATURE [Part::Feature] Shape031  label="D35_LED_0805_2012Metric_5FD6A49F"
  Placement = pos=(80.01,-77.47,0) rot=(0,0,1;3.14159rad)
  shape: bbox 2 x 1.25 x 1.1 mm, 50 faces (baked)
FEATURE [Part::Feature] Shape032  label="D36_LED_0805_2012Metric_5FD6ABEF"
  Placement = pos=(196.215,-65.786,0) rot=(0,0,1;1.5708rad)
  shape: bbox 1.25 x 2 x 1.1 mm, 50 faces (baked)
FEATURE [Part::Feature] Shape033  label="P1_PinHeader_1x04_P254mm_Vertical_SMD_Pin1Left_5FD6AC81"
  Placement = pos=(50.8,-78.74,0) rot=(0,0,1;0rad)
  shape: bbox 5 x 10.16 x 9.3 mm, 112 faces (baked)
FEATURE [Part::Feature] Shape034  label="P2_PinHeader_1x06_P254mm_Vertical_SMD_Pin1Left_5FD6AB52"
  Placement = pos=(175.26,-63.5,0) rot=(0,0,-1;1.5708rad)
  shape: bbox 15.24 x 5 x 9.3 mm, 166 faces (baked)
FEATURE [Part::Feature] Shape035  label="R2_R_0805_2012Metric_5FD6B2E7"
  Placement = pos=(175.895,-88.9,0) rot=(0,0,1;1.5708rad)
  shape: bbox 1.2 x 2 x 0.45 mm, 26 faces (baked)
FEATURE [Part::Feature] Shape036  label="R3_R_0805_2012Metric_5FD6AC33"
  Placement = pos=(178.435,-88.9,0) rot=(0,0,1;1.5708rad)
  shape: bbox 1.2 x 2 x 0.45 mm, 26 faces (baked)
FEATURE [Part::Feature] Shape037  label="R4_R_0805_2012Metric_5FD6AAA1"
  Placement = pos=(191.135,-88.9,0) rot=(0,0,1;1.5708rad)
  shape: bbox 1.2 x 2 x 0.45 mm, 26 faces (baked)
FEATURE [Part::Feature] Shape038  label="R5_R_0805_2012Metric_5FD6A4DA"
  Placement = pos=(165.735,-80.645,0) rot=(0,0,1;1.5708rad)
  shape: bbox 1.2 x 2 x 0.45 mm, 26 faces (baked)
FEATURE [Part::Feature] Shape039  label="R6_R_0805_2012Metric_5FD6A339"
  Placement = pos=(165.735,-76.835,0) rot=(0,0,-1;1.5708rad)
  shape: bbox 1.2 x 2 x 0.45 mm, 26 faces (baked)
FEATURE [Part::Feature] Shape040  label="R7_R_0805_2012Metric_5FD6B317"
  Placement = pos=(80.01,-74.93,0) rot=(0,0,1;3.14159rad)
  shape: bbox 2 x 1.2 x 0.45 mm, 26 faces (baked)
FEATURE [Part::Feature] Shape041  label="U1_TQFP_32_7x7mm_P08mm_5FD69531"
  Placement = pos=(190.59,-78.8298,0) rot=(0,0,1;2.35619rad)
  shape: bbox 10.59 x 10.59 x 1.1 mm, 524 faces (baked)
FEATURE [Part::Feature] Shape042  label="X1_Crystal_SMD_3225-4Pin_3.2x2.5mm_5FD6AF07"
  Placement = pos=(201.295,-76.962,0) rot=(0,0,1;1.5708rad)
  shape: bbox 2.501 x 3.2 x 0.64 mm, 28 faces (baked)
FEATURE [Part::Feature] Shape043  label="SW2_PinHeader_2x02_P254mm_Vertical_SMD_5FD6B28B"
  Placement = pos=(187.96,-118.11,0) rot=(0,0,1;3.14159rad)
  shape: bbox 7.54 x 5.08 x 9.3 mm, 100 faces (baked)
FEATURE [Part::Feature] Shape044  label="D34_D_SMB_5FD6B233"
  Placement = pos=(119.38,-76.2,0) rot=(0,0,1;0rad)
  shape: bbox 5.3 x 3.55 x 2.15 mm, 41 faces (baked)
FEATURE [Part::Feature] Shape045  label="C19_C_0805_2012Metric_5FD6B1B2"
  Placement = pos=(80.01,-82.55,0) rot=(0,0,1;3.14159rad)
  shape: bbox 2 x 1.25 x 1.25 mm, 28 faces (baked)
FEATURE [Part::Feature] Shape046  label="R9_R_0805_2012Metric_5FD6B182"
  Placement = pos=(71.12,-77.47,0) rot=(0,0,1;0rad)
  shape: bbox 2 x 1.2 x 0.45 mm, 26 faces (baked)
FEATURE [Part::Feature] Shape047  label="R10_R_0805_2012Metric_5FD6B152"
  Placement = pos=(71.12,-80.01,0) rot=(0,0,1;0rad)
  shape: bbox 2 x 1.2 x 0.45 mm, 26 faces (baked)
FEATURE [Part::Feature] Shape048  label="C22_C_0805_2012Metric_5FD6B0B0"
  Placement = pos=(168.91,-114.3,0) rot=(0,0,1;1.5708rad)
  shape: bbox 1.25 x 2 x 1.25 mm, 28 faces (baked)
FEATURE [Part::Feature] Shape049  label="C23_C_0805_2012Metric_5FD6B080"
  Placement = pos=(181.61,-88.9,0) rot=(0,0,-1;1.5708rad)
  shape: bbox 1.25 x 2 x 1.25 mm, 28 faces (baked)
FEATURE [Part::Feature] Shape050  label="C24_C_0805_2012Metric_5FD6B050"
  Placement = pos=(199.39,-114.3,0) rot=(0,0,1;1.5708rad)
  shape: bbox 1.25 x 2 x 1.25 mm, 28 faces (baked)
FEATURE [Part::Feature] Shape051  label="C25_C_0805_2012Metric_5FD6B020"
  Placement = pos=(229.87,-114.3,0) rot=(0,0,1;1.5708rad)
  shape: bbox 1.25 x 2 x 1.25 mm, 28 faces (baked)
FEATURE [Part::Feature] Shape052  label="C26_C_0805_2012Metric_5FD6AFF0"
  Placement = pos=(227.838,-88.9,0) rot=(0,0,-1;1.5708rad)
  shape: bbox 1.25 x 2 x 1.25 mm, 28 faces (baked)
FEATURE [Part::Feature] Shape053  label="D41_LED_WS2812B_PLCC4_50x50mm_P32mm_5FCECC3E"
  Placement = pos=(158.75,-98.425,0) rot=(0,0,1;0rad)
  shape: bbox 5.4 x 5 x 1.6 mm, 68 faces (baked)
FEATURE [Part::Feature] Shape054  label="D42_LED_WS2812B_PLCC4_50x50mm_P32mm_5FCECC56"
  Placement = pos=(158.75,-104.775,0) rot=(0,0,1;0rad)
  shape: bbox 5.4 x 5 x 1.6 mm, 68 faces (baked)
FEATURE [Part::Feature] Shape055  label="D43_LED_WS2812B_PLCC4_50x50mm_P32mm_5FCECC6E"
  Placement = pos=(166.37,-104.775,0) rot=(0,0,1;3.14159rad)
  shape: bbox 5.4 x 5 x 1.6 mm, 68 faces (baked)
FEATURE [Part::Feature] Shape056  label="D44_LED_WS2812B_PLCC4_50x50mm_P32mm_5FCECC86"
  Placement = pos=(166.37,-98.425,0) rot=(0,0,1;3.14159rad)
  shape: bbox 5.4 x 5 x 1.6 mm, 68 faces (baked)
FEATURE [Part::Feature] Shape057  label="D45_LED_WS2812B_PLCC4_50x50mm_P32mm_5FCECC9E"
  Placement = pos=(173.99,-98.425,0) rot=(0,0,1;0rad)
  shape: bbox 5.4 x 5 x 1.6 mm, 68 faces (baked)
FEATURE [Part::Feature] Shape058  label="D48_LED_WS2812B_PLCC4_50x50mm_P32mm_5FCECCE6"
  Placement = pos=(181.61,-98.425,0) rot=(0,0,1;3.14159rad)
  shape: bbox 5.4 x 5 x 1.6 mm, 68 faces (baked)
FEATURE [Part::Feature] Shape059  label="D49_LED_WS2812B_PLCC4_50x50mm_P32mm_5FCECCFE"
  Placement = pos=(189.23,-98.425,0) rot=(0,0,1;0rad)
  shape: bbox 5.4 x 5 x 1.6 mm, 68 faces (baked)
FEATURE [Part::Feature] Shape060  label="D50_LED_WS2812B_PLCC4_50x50mm_P32mm_5FCECD16"
  Placement = pos=(189.23,-104.775,0) rot=(0,0,1;0rad)
  shape: bbox 5.4 x 5 x 1.6 mm, 68 faces (baked)
FEATURE [Part::Feature] Shape061  label="D51_LED_WS2812B_PLCC4_50x50mm_P32mm_5FCECD2E"
  Placement = pos=(196.85,-104.775,0) rot=(0,0,1;3.14159rad)
  shape: bbox 5.4 x 5 x 1.6 mm, 68 faces (baked)
FEATURE [Part::Feature] Shape062  label="D52_LED_WS2812B_PLCC4_50x50mm_P32mm_5FCECD46"
  Placement = pos=(196.85,-98.425,0) rot=(0,0,1;3.14159rad)
  shape: bbox 5.4 x 5 x 1.6 mm, 68 faces (baked)
FEATURE [Part::Feature] Shape063  label="D60_LED_WS2812B_PLCC4_50x50mm_P32mm_5FCECE06"
  Placement = pos=(227.33,-98.425,0) rot=(0,0,1;3.14159rad)
  shape: bbox 5.4 x 5 x 1.6 mm, 68 faces (baked)
FEATURE [Part::Feature] Shape064  label="D61_LED_WS2812B_PLCC4_50x50mm_P32mm_5FCECE1E"
  Placement = pos=(234.95,-98.425,0) rot=(0,0,1;0rad)
  shape: bbox 5.4 x 5 x 1.6 mm, 68 faces (baked)
FEATURE [Part::Feature] Shape065  label="D62_LED_WS2812B_PLCC4_50x50mm_P32mm_5FCECE36"
  Placement = pos=(234.95,-104.775,0) rot=(0,0,1;0rad)
  shape: bbox 5.4 x 5 x 1.6 mm, 68 faces (baked)
FEATURE [Part::Feature] Shape066  label="D63_LED_WS2812B_PLCC4_50x50mm_P32mm_5FCECE4E"
  Placement = pos=(242.57,-104.775,0) rot=(0,0,1;3.14159rad)
  shape: bbox 5.4 x 5 x 1.6 mm, 68 faces (baked)
FEATURE [Part::Feature] Shape067  label="D67_LED_WS2812B_PLCC4_50x50mm_P32mm_5FCECEAE"
  Placement = pos=(257.81,-104.775,0) rot=(0,0,1;3.14159rad)
  shape: bbox 5.4 x 5 x 1.6 mm, 68 faces (baked)
FEATURE [Part::Feature] Shape068  label="D68_LED_WS2812B_PLCC4_50x50mm_P32mm_5FCECEC6"
  Placement = pos=(257.81,-98.425,0) rot=(0,0,1;3.14159rad)
  shape: bbox 5.4 x 5 x 1.6 mm, 68 faces (baked)
FEATURE [Part::Feature] Shape069  label="P6_PinHeader_2x04_P254mm_Vertical_SMD_5FD6A833"
  Placement = pos=(158.115,-76.835,0) rot=(0,0,1;1.5708rad)
  shape: bbox 10.16 x 7.54 x 9.3 mm, 196 faces (baked)
FEATURE [Part::Feature] Shape070  label="SW1_SW_SPST_PTS645_5FD6A5D7[2]"
  Placement = pos=(172.72,-76.2,0) rot=(0,0,1;3.14159rad)
  shape: bbox 9 x 6 x 4.3 mm, 97 faces (baked)
FEATURE [Part::Feature] Shape071  label="D1_LED_WS2812B_PLCC4_50x50mm_P32mm_5FD31A7E"
  Placement = pos=(21.59,-98.425,0) rot=(0,0,1;0rad)
  shape: bbox 5.4 x 5 x 1.6 mm, 68 faces (baked)
FEATURE [Part::Feature] Shape072  label="C12_C_0805_2012Metric_5FD6A468"
  Placement = pos=(62.23,-114.3,0) rot=(0,0,1;1.5708rad)
  shape: bbox 1.25 x 2 x 1.25 mm, 28 faces (baked)
FEATURE [Part::Feature] Shape073  label="C13_C_0805_2012Metric_5FD6A438"
  Placement = pos=(74.93,-88.9,0) rot=(0,0,-1;1.5708rad)
  shape: bbox 1.25 x 2 x 1.25 mm, 28 faces (baked)
FEATURE [Part::Feature] Shape074  label="C14_C_0805_2012Metric_5FD6A408"
  Placement = pos=(92.71,-114.3,0) rot=(0,0,1;1.5708rad)
  shape: bbox 1.25 x 2 x 1.25 mm, 28 faces (baked)
FEATURE [Part::Feature] Shape075  label="C15_C_0805_2012Metric_5FD6A3D8"
  Placement = pos=(105.41,-88.9,0) rot=(0,0,-1;1.5708rad)
  shape: bbox 1.25 x 2 x 1.25 mm, 28 faces (baked)
FEATURE [Part::Feature] Shape076  label="C16_C_0805_2012Metric_5FD6A6CC"
  Placement = pos=(107.95,-114.3,0) rot=(0,0,1;1.5708rad)
  shape: bbox 1.25 x 2 x 1.25 mm, 28 faces (baked)
FEATURE [Part::Feature] Shape077  label="C21_C_0805_2012Metric_5FD6A69C"
  Placement = pos=(151.13,-88.9,0) rot=(0,0,-1;1.5708rad)
  shape: bbox 1.25 x 2 x 1.25 mm, 28 faces (baked)
FEATURE [Part::Feature] Shape078  label="D5_LED_WS2812B_PLCC4_50x50mm_P32mm_5FD28A06"
  Placement = pos=(36.83,-98.425,0) rot=(0,0,1;0rad)
  shape: bbox 5.4 x 5 x 1.6 mm, 68 faces (baked)
FEATURE [Part::Feature] Shape079  label="D6_LED_WS2812B_PLCC4_50x50mm_P32mm_5FD28A1E"
  Placement = pos=(36.83,-104.775,0) rot=(0,0,1;0rad)
  shape: bbox 5.4 x 5 x 1.6 mm, 68 faces (baked)
FEATURE [Part::Feature] Shape080  label="D7_LED_WS2812B_PLCC4_50x50mm_P32mm_5FD28A36"
  Placement = pos=(44.45,-104.775,0) rot=(0,0,1;3.14159rad)
  shape: bbox 5.4 x 5 x 1.6 mm, 68 faces (baked)
FEATURE [Part::Feature] Shape081  label="D8_LED_WS2812B_PLCC4_50x50mm_P32mm_5FD28A4E"
  Placement = pos=(44.45,-98.425,0) rot=(0,0,1;3.14159rad)
  shape: bbox 5.4 x 5 x 1.6 mm, 68 faces (baked)
FEATURE [Part::Feature] Shape082  label="D9_LED_WS2812B_PLCC4_50x50mm_P32mm_5FD28A66"
  Placement = pos=(52.07,-98.425,0) rot=(0,0,1;0rad)
  shape: bbox 5.4 x 5 x 1.6 mm, 68 faces (baked)
FEATURE [Part::Feature] Shape083  label="D12_LED_WS2812B_PLCC4_50x50mm_P32mm_5FD28A7E"
  Placement = pos=(59.69,-98.425,0) rot=(0,0,1;3.14159rad)
  shape: bbox 5.4 x 5 x 1.6 mm, 68 faces (baked)
FEATURE [Part::Feature] Shape084  label="D13_LED_WS2812B_PLCC4_50x50mm_P32mm_5FD28A96"
  Placement = pos=(67.31,-98.425,0) rot=(0,0,1;0rad)
  shape: bbox 5.4 x 5 x 1.6 mm, 68 faces (baked)
FEATURE [Part::Feature] Shape085  label="D14_LED_WS2812B_PLCC4_50x50mm_P32mm_5FD28AAE"
  Placement = pos=(67.31,-104.775,0) rot=(0,0,1;0rad)
  shape: bbox 5.4 x 5 x 1.6 mm, 68 faces (baked)
FEATURE [Part::Feature] Shape086  label="D15_LED_WS2812B_PLCC4_50x50mm_P32mm_5FD28AC6"
  Placement = pos=(74.93,-104.775,0) rot=(0,0,1;3.14159rad)
  shape: bbox 5.4 x 5 x 1.6 mm, 68 faces (baked)
FEATURE [Part::Feature] Shape087  label="D16_LED_WS2812B_PLCC4_50x50mm_P32mm_5FD28ADE"
  Placement = pos=(74.93,-98.425,0) rot=(0,0,1;3.14159rad)
  shape: bbox 5.4 x 5 x 1.6 mm, 68 faces (baked)
FEATURE [Part::Feature] Shape088  label="D24_LED_WS2812B_PLCC4_50x50mm_P32mm_5FD28AF6"
  Placement = pos=(105.41,-98.425,0) rot=(0,0,1;3.14159rad)
  shape: bbox 5.4 x 5 x 1.6 mm, 68 faces (baked)
FEATURE [Part::Feature] Shape089  label="D25_LED_WS2812B_PLCC4_50x50mm_P32mm_5FD28B0E"
  Placement = pos=(113.03,-98.425,0) rot=(0,0,1;0rad)
  shape: bbox 5.4 x 5 x 1.6 mm, 68 faces (baked)
FEATURE [Part::Feature] Shape090  label="D26_LED_WS2812B_PLCC4_50x50mm_P32mm_5FD28B26"
  Placement = pos=(113.03,-104.775,0) rot=(0,0,1;0rad)
  shape: bbox 5.4 x 5 x 1.6 mm, 68 faces (baked)
FEATURE [Part::Feature] Shape091  label="D27_LED_WS2812B_PLCC4_50x50mm_P32mm_5FD28B3E"
  Placement = pos=(120.65,-104.775,0) rot=(0,0,1;3.14159rad)
  shape: bbox 5.4 x 5 x 1.6 mm, 68 faces (baked)
FEATURE [Part::Feature] Shape092  label="D31_LED_WS2812B_PLCC4_50x50mm_P32mm_5FD28B56"
  Placement = pos=(135.89,-104.775,0) rot=(0,0,1;3.14159rad)
  shape: bbox 5.4 x 5 x 1.6 mm, 68 faces (baked)
FEATURE [Part::Feature] Shape093  label="D32_LED_WS2812B_PLCC4_50x50mm_P32mm_5FD28B6E"
  Placement = pos=(135.89,-98.425,0) rot=(0,0,1;3.14159rad)
  shape: bbox 5.4 x 5 x 1.6 mm, 68 faces (baked)
FEATURE [Part::Feature] Shape094  label="D37_LED_WS2812B_PLCC4_50x50mm_P32mm_5FD28B86"
  Placement = pos=(143.51,-98.425,0) rot=(0,0,1;0rad)
  shape: bbox 5.4 x 5 x 1.6 mm, 68 faces (baked)
FEATURE [Part::Feature] Shape095  label="D38_LED_WS2812B_PLCC4_50x50mm_P32mm_5FD28B9E"
  Placement = pos=(143.51,-104.775,0) rot=(0,0,1;0rad)
  shape: bbox 5.4 x 5 x 1.6 mm, 68 faces (baked)
FEATURE [Part::Feature] Shape096  label="D39_LED_WS2812B_PLCC4_50x50mm_P32mm_5FD28BB6"
  Placement = pos=(151.13,-104.775,0) rot=(0,0,1;3.14159rad)
  shape: bbox 5.4 x 5 x 1.6 mm, 68 faces (baked)
FEATURE [Part::Feature] Shape097  label="D40_LED_WS2812B_PLCC4_50x50mm_P32mm_5FD28BCE"
  Placement = pos=(151.13,-98.425,0) rot=(0,0,1;3.14159rad)
  shape: bbox 5.4 x 5 x 1.6 mm, 68 faces (baked)
FEATURE [Part::Feature] Shape098  label="D46_LED_WS2812B_PLCC4_50x50mm_P32mm_5FD33BA2"
  Placement = pos=(173.99,-104.775,0) rot=(0,0,1;0rad)
  shape: bbox 5.4 x 5 x 1.6 mm, 68 faces (baked)
FEATURE [Part::Feature] Shape099  label="D47_LED_WS2812B_PLCC4_50x50mm_P32mm_5FD28BFE"
  Placement = pos=(181.61,-104.775,0) rot=(0,0,1;3.14159rad)
  shape: bbox 5.4 x 5 x 1.6 mm, 68 faces (baked)
FEATURE [Part::Feature] Shape100  label="D53_LED_WS2812B_PLCC4_50x50mm_P32mm_5FD28C16"
  Placement = pos=(204.47,-98.425,0) rot=(0,0,1;0rad)
  shape: bbox 5.4 x 5 x 1.6 mm, 68 faces (baked)
FEATURE [Part::Feature] Shape101  label="D54_LED_WS2812B_PLCC4_50x50mm_P32mm_5FD28C2E"
  Placement = pos=(204.47,-104.775,0) rot=(0,0,1;0rad)
  shape: bbox 5.4 x 5 x 1.6 mm, 68 faces (baked)
FEATURE [Part::Feature] Shape102  label="D55_LED_WS2812B_PLCC4_50x50mm_P32mm_5FD28C46"
  Placement = pos=(212.09,-104.775,0) rot=(0,0,1;3.14159rad)
  shape: bbox 5.4 x 5 x 1.6 mm, 68 faces (baked)
FEATURE [Part::Feature] Shape103  label="D56_LED_WS2812B_PLCC4_50x50mm_P32mm_5FD28C5E"
  Placement = pos=(212.09,-98.425,0) rot=(0,0,1;3.14159rad)
  shape: bbox 5.4 x 5 x 1.6 mm, 68 faces (baked)
FEATURE [Part::Feature] Shape104  label="D57_LED_WS2812B_PLCC4_50x50mm_P32mm_5FD28C76"
  Placement = pos=(219.71,-98.425,0) rot=(0,0,1;0rad)
  shape: bbox 5.4 x 5 x 1.6 mm, 68 faces (baked)
FEATURE [Part::Feature] Shape105  label="D58_LED_WS2812B_PLCC4_50x50mm_P32mm_5FD28C8E"
  Placement = pos=(219.71,-104.775,0) rot=(0,0,1;0rad)
  shape: bbox 5.4 x 5 x 1.6 mm, 68 faces (baked)
FEATURE [Part::Feature] Shape106  label="D59_LED_WS2812B_PLCC4_50x50mm_P32mm_5FD28CA6"
  Placement = pos=(227.33,-104.775,0) rot=(0,0,1;3.14159rad)
  shape: bbox 5.4 x 5 x 1.6 mm, 68 faces (baked)
FEATURE [Part::Feature] Shape107  label="D64_LED_WS2812B_PLCC4_50x50mm_P32mm_5FD3436E"
  Placement = pos=(242.57,-98.425,0) rot=(0,0,1;3.14159rad)
  shape: bbox 5.4 x 5 x 1.6 mm, 68 faces (baked)
FEATURE [Part::Feature] Shape108  label="D65_LED_WS2812B_PLCC4_50x50mm_P32mm_5FD28CD6"
  Placement = pos=(250.19,-98.425,0) rot=(0,0,1;0rad)
  shape: bbox 5.4 x 5 x 1.6 mm, 68 faces (baked)
FEATURE [Part::Feature] Shape109  label="P4_PinHeader_1x04_P254mm_Vertical_SMD_Pin1Left_5FD6AF5D"
  Placement = pos=(228.6,-78.74,0) rot=(0,0,1;0rad)
  shape: bbox 5 x 10.16 x 9.3 mm, 112 faces (baked)
FEATURE [Part::Feature] Shape110  label="D66_LED_WS2812B_PLCC4_50x50mm_P32mm_5FD34DB7"
  Placement = pos=(250.19,-104.775,0) rot=(0,0,1;0rad)
  shape: bbox 5.4 x 5 x 1.6 mm, 68 faces (baked)
FEATURE [Part::Feature] Shape111  label="C1_CP_Elec_63x77_5FD6AA2B"
  Placement = pos=(204.47,-86.995,0) rot=(0,0,1;0rad)
  shape: bbox 8.606 x 8.603 x 7.7 mm, 41 faces (baked)
FEATURE [Part::Feature] Shape112  label="C7_CP_Elec_63x77_5FD6A9B6"
  Placement = pos=(99.695,-72.39,0) rot=(0,0,1;1.5708rad)
  shape: bbox 8.603 x 8.606 x 7.7 mm, 41 faces (baked)
FEATURE [Part::Feature] Shape113  label="C27_CP_Elec_63x77_5FD6A941"
  Placement = pos=(60.96,-72.39,0) rot=(0,0,1;1.5708rad)
  shape: bbox 8.603 x 8.606 x 7.7 mm, 41 faces (baked)
FEATURE [Part::Feature] Part__Feature024  label="conn_barrel"
  shape: bbox 7.831 x 8 x 4.6 mm, 23 faces (baked)
FEATURE [Part::Feature] Part__Feature025  label="conn_barrel001"
  shape: bbox 2.383 x 4.6 x 15.3 mm, 26 faces (baked)
FEATURE [Part::Feature] Part__Feature026  label="conn_barrel002"
  shape: bbox 2.5 x 4.2 x 19.45 mm, 17 faces (baked)
FEATURE [Part::Feature] Part__Feature027  label="conn_barrel003"
  shape: bbox 10 x 10 x 13.9 mm, 55 faces (baked)
FEATURE [App::Part] conn_barrel  label="J1_conn_barrel004_5FD6968E"
  Group = -> [Part__Feature024,Part__Feature025,Part__Feature026,Part__Feature027]
  Origin = -> Origin159
  Placement = pos=(139.7,-68.58,0) rot=(0,0,1;0rad)
FEATURE [App::Part] Top_a344
  Group = -> [Shape,barrel_jack_DC_005_5A_2_5_SMT,sparkfun_apds_9960,USB4110_GF_A018_cp,Shape001,Shape002,Shape003,Shape004,Shape005,Shape006,Shape007,Shape008,Shape009,Shape010,Shape011,Shape012,Shape013,Shape014,Shape015,Shape016,Shape017,Shape018,Shape019,Shape020,Shape021,Shape022,Shape023,Shape024,Shape025,Shape026,Shape027,Shape028,Shape029,Shape030,Shape031,Shape032,Shape033,Shape034,Shape035,Shape036,+78 more]
  Origin = -> Origin151
FEATURE [App::Part] Step_Models_a344
  Group = -> [Top_a344]
  Origin = -> Origin150
FEATURE [App::Part] Board_a344  label="halo"
  Group = -> [Board_Geoms_a344,Step_Models_a344]
  Origin = -> Origin149
  Placement = pos=(-139.7,101.6,1.6) rot=(0,0,1;0rad)
FEATURE [Sketcher::SketchObject] Sketch021
  ExternalGeometry = -> [ShapeBinder005,ShapeBinder004]
  FullyConstrained = true
  MapMode = 5
  Support = -> [XY_Plane161]
  sketch-geometry (8):
    g0: LineSegment StartX=-111.5 StartY=-46.1898 StartZ=0 EndX=111.5 EndY=-46.1898 EndZ=0
    g1: LineSegment StartX=111.5 StartY=-46.1898 StartZ=0 EndX=111.5 EndY=-43.1898 EndZ=0
    g2: LineSegment StartX=111.5 StartY=-43.1898 StartZ=0 EndX=-111.5 EndY=-43.1898 EndZ=0
    g3: LineSegment StartX=-111.5 StartY=-43.1898 StartZ=0 EndX=-111.5 EndY=-46.1898 EndZ=0
    g4: LineSegment StartX=111.5 StartY=-43.1898 StartZ=0 EndX=111.8 EndY=-43.1398 EndZ=0
    g5: LineSegment StartX=111.5 StartY=-46.1898 StartZ=0 EndX=111.8 EndY=-46.2398 EndZ=0
    g6: LineSegment StartX=-111.5 StartY=-46.1898 StartZ=0 EndX=-111.8 EndY=-46.2398 EndZ=0
    g7: LineSegment StartX=-111.5 StartY=-43.1898 StartZ=0 EndX=-111.8 EndY=-43.1398 EndZ=0
  constraints (20):
    c: Coincident(g0,g1)
    c: Coincident(g1,g2)
    c: Coincident(g2,g3)
    c: Coincident(g3,g0)
    c: Horizontal(g0)
    c: Horizontal(g2)
    c: Vertical(g1)
    c: Coincident(g4,g1)
    c: Coincident(g4,g-4)
    c: Coincident(g5,g0)
    c: Coincident(g5,g-4)
    c: Coincident(g6,g0)
    c: Coincident(g6,g-3)
    c: Coincident(g7,g2)
    c: Coincident(g7,g-3)
    c: Equal(g6,g7)
    c: Equal(g7,g4)
    c: Equal(g4,g5)
    c: DistanceY(g1,g1) = 3
    c: DistanceX(g0,g0) = 223
FEATURE [PartDesign::Pad] Pad022
  Direction = (1,1,1)
  Length = 20
  Length2 = 100
  Profile = -> Sketch021
  Type = 0
FEATURE [Sketcher::SketchObject] Sketch022
  FullyConstrained = true
  MapMode = 5
  Placement = pos=(0,-43.1898,0) rot=(0,0.707107,0.707107;3.14159rad)
  Support = -> [Pad022]
  sketch-geometry (5):
    g0: LineSegment StartX=16.205 StartY=12.9 StartZ=0 EndX=25.705 EndY=12.9 EndZ=0
    g1: LineSegment StartX=25.705 StartY=12.9 StartZ=0 EndX=25.705 EndY=1.4 EndZ=0
    g2: LineSegment StartX=25.705 StartY=1.4 StartZ=0 EndX=16.205 EndY=1.4 EndZ=0
    g3: LineSegment StartX=16.205 StartY=1.4 StartZ=0 EndX=16.205 EndY=12.9 EndZ=0
    g4: LineSegment StartX=20.955 StartY=12.9 StartZ=0 EndX=20.955 EndY=1.4 EndZ=0
  constraints (15):
    c: Coincident(g0,g1)
    c: Coincident(g1,g2)
    c: Coincident(g2,g3)
    c: Coincident(g3,g0)
    c: Horizontal(g0)
    c: Horizontal(g2)
    c: Vertical(g1)
    c: Vertical(g3)
    c: PointOnObject(g4,g0)
    c: PointOnObject(g4,g2)
    c: Symmetric(g0,g0,g4)
    c: DistanceX(g0,g0) = 9.5
    c: DistanceY(g3,g3) = 11.5
    c: DistanceX(g-1,g4) = 20.955
    c: DistanceY(g-1,g4) = 1.4
FEATURE [PartDesign::Pocket] Pocket
  BaseFeature = -> Pad022
  Direction = (1,1,1)
  Length = 5
  Length2 = 100
  Profile = -> Sketch022
  Type = 1
FEATURE [Sketcher::SketchObject] Sketch023
  FullyConstrained = true
  MapMode = 5
  Placement = pos=(0,-43.1898,0) rot=(0,0.707107,0.707107;3.14159rad)
  Support = -> [Pocket]
  sketch-geometry (9):
    g0: LineSegment StartX=-23.415 StartY=6.5 StartZ=0 EndX=-13.415 EndY=6.5 EndZ=0
    g1: LineSegment StartX=-12.415 StartY=5.5 StartZ=0 EndX=-12.415 EndY=-0.5 EndZ=0
    g2: LineSegment StartX=-13.415 StartY=-1.5 StartZ=0 EndX=-23.415 EndY=-1.5 EndZ=0
    g3: LineSegment StartX=-24.415 StartY=-0.5 StartZ=0 EndX=-24.415 EndY=5.5 EndZ=0
    g4: ArcOfCircle CenterX=-23.415 CenterY=5.5 CenterZ=0 NormalX=0 NormalY=0 NormalZ=1 AngleXU=0 Radius=1 StartAngle=1.5708 EndAngle=3.14159
    g5: ArcOfCircle CenterX=-23.415 CenterY=-0.5 CenterZ=0 NormalX=0 NormalY=0 NormalZ=1 AngleXU=0 Radius=1 StartAngle=3.14159 EndAngle=4.71239
    g6: ArcOfCircle CenterX=-13.415 CenterY=-0.5 CenterZ=0 NormalX=0 NormalY=0 NormalZ=1 AngleXU=0 Radius=1 StartAngle=4.71239 EndAngle=6.28319
    g7: ArcOfCircle CenterX=-13.415 CenterY=5.5 CenterZ=0 NormalX=0 NormalY=0 NormalZ=1 AngleXU=0 Radius=1 StartAngle=0 EndAngle=1.5708
    g8: LineSegment StartX=-18.415 StartY=6.5 StartZ=0 EndX=-18.415 EndY=-1.5 EndZ=0
  constraints (23):
    c: Horizontal(g0)
    c: Horizontal(g2)
    c: Vertical(g1)
    c: Vertical(g3)
    c: Tangent(g0,g4) = 1.5708
    c: Tangent(g3,g4) = 1.5708
    c: Tangent(g3,g5) = 1.5708
    c: Tangent(g2,g5) = 1.5708
    c: Tangent(g2,g6) = 1.5708
    c: Tangent(g1,g6) = 1.5708
    c: Tangent(g1,g7) = 1.5708
    c: Tangent(g0,g7) = 1.5708
    c: DistanceX(g3,g1) = 12
    c: DistanceY(g2,g0) = 8
    c: Radius(g4) = 1
    c: Equal(g4,g7)
    c: Equal(g4,g6)
    c: Equal(g4,g5)
    c: PointOnObject(g8,g0)
    c: PointOnObject(g8,g2)
    c: Symmetric(g3,g1,g8)
    c: DistanceX(g8,g-1) = 18.415
    c: DistanceY(g-1,g8) = 6.5
FEATURE [PartDesign::Pocket] Pocket001
  BaseFeature = -> Pocket
  Direction = (1,1,1)
  Length = 5
  Length2 = 100
  Profile = -> Sketch023
  Type = 1
FEATURE [PartDesign::Body] Body013  label="ACR_wall_back"
  Group = -> [Sketch021,Pad022,Sketch022,Pocket,Sketch023,Pocket001]
  Origin = -> Origin160
  Placement = pos=(0,88.392,0) rot=(0,0,1;0rad)
  Tip = -> Pocket001
FEATURE [Sketcher::SketchObject] Sketch024
  FullyConstrained = true
  MapMode = 5
  Support = -> [XY_Plane162]
  expr: Constraints[25] = 48.26 mm - 1 mm - 12.7 mm
  sketch-geometry (11):
    g0: LineSegment StartX=-105.37 StartY=46.6624 StartZ=0 EndX=-105.37 EndY=45.264 EndZ=0
    g1: LineSegment StartX=-105.37 StartY=45.264 StartZ=0 EndX=-111.87 EndY=45.264 EndZ=0
    g2: LineSegment StartX=-111.87 StartY=45.264 StartZ=0 EndX=-111.87 EndY=42.164 EndZ=0
    g3: LineSegment StartX=-111.87 StartY=42.164 StartZ=0 EndX=-105.37 EndY=42.164 EndZ=0
    g4: LineSegment StartX=-105.37 StartY=42.164 StartZ=0 EndX=-105.37 EndY=7.36 EndZ=0
    g5: ArcOfCircle CenterX=-106.17 CenterY=7.36 CenterZ=0 NormalX=0 NormalY=0 NormalZ=1 AngleXU=0 Radius=0.8 StartAngle=4.71239 EndAngle=6.28319
    g6: LineSegment StartX=-106.17 StartY=6.56 StartZ=0 EndX=-121.92 EndY=6.56 EndZ=0
    g7: LineSegment StartX=-121.92 StartY=6.56 StartZ=0 EndX=-121.92 EndY=34.56 EndZ=0
    g8: ArcOfCircle CenterX=-109.22 CenterY=34.56 CenterZ=0 NormalX=0 NormalY=0 NormalZ=1 AngleXU=0 Radius=12.7 StartAngle=1.2628 EndAngle=3.14159
    g9: Circle CenterX=-109.22 CenterY=34.56 CenterZ=0 NormalX=0 NormalY=0 NormalZ=1 AngleXU=0 Radius=2.4
    g10: Circle CenterX=-109.22 CenterY=18.46 CenterZ=0 NormalX=0 NormalY=0 NormalZ=1 AngleXU=0 Radius=2.4
  constraints (31):
    c: Coincident(g0,g1)
    c: Coincident(g1,g2)
    c: Coincident(g2,g3)
    c: Horizontal(g3)
    c: Coincident(g3,g4)
    c: Vertical(g4)
    c: Tangent(g4,g5) = 1.5708
    c: Horizontal(g6)
    c: Coincident(g6,g7)
    c: Vertical(g7)
    c: Tangent(g7,g8) = 1.5708
    c: Coincident(g8,g0)
    c: Horizontal(g1)
    c: DistanceY(g2,g2) = 3.1
    c: Vertical(g2)
    c: Equal(g1,g3)
    c: DistanceX(g1,g1) = 6.5
    c: Radius(g5) = 0.8
    c: Tangent(g5,g6) = 1.5708
    c: Radius(g8) = 12.7
    c: Vertical(g0)
    c: DistanceX(g6,g6) = 15.75
    c: DistanceY(g7,g7) = 28
    c: DistanceY(g-1,g2) = 42.164
    c: DistanceX(g6,g-1) = 121.92
    c: DistanceY(g-1,g8) = 34.56
    c: Equal(g10,g9)
    c: Radius(g9) = 2.4
    c: Coincident(g9,g8)
    c: DistanceX(g8,g10) = 0
    c: DistanceY(g10,g8) = 16.1
FEATURE [PartDesign::Pad] Pad023
  Direction = (1,1,1)
  Length = 20
  Length2 = 100
  Profile = -> Sketch024
  Type = 0
FEATURE [Sketcher::SketchObject] Sketch025
  ExternalGeometry = -> [Pad023]
  FullyConstrained = true
  MapMode = 5
  Placement = pos=(0,0,20) rot=(0,0,1;0rad)
  Support = -> [Pad023]
  sketch-geometry (4):
    g0: LineSegment StartX=-105.37 StartY=42.164 StartZ=0 EndX=-102.87 EndY=42.164 EndZ=0
    g1: LineSegment StartX=-102.87 StartY=42.164 StartZ=0 EndX=-102.87 EndY=7.36 EndZ=0
    g2: LineSegment StartX=-102.87 StartY=7.36 StartZ=0 EndX=-105.37 EndY=7.36 EndZ=0
    g3: LineSegment StartX=-105.37 StartY=7.36 StartZ=0 EndX=-105.37 EndY=42.164 EndZ=0
  constraints (10):
    c: Coincident(g0,g1)
    c: Coincident(g1,g2)
    c: Coincident(g2,g3)
    c: Coincident(g3,g0)
    c: Horizontal(g0)
    c: Horizontal(g2)
    c: Vertical(g1)
    c: DistanceX(g2,g2) = 2.5
    c: Coincident(g0,g-3)
    c: Coincident(g2,g-3)
FEATURE [PartDesign::Pad] Pad024
  BaseFeature = -> Pad023
  Direction = (1,1,1)
  Length = 18.3
  Length2 = 100
  Profile = -> Sketch025
  Refine = true
  Reversed = true
  Type = 0
FEATURE [PartDesign::ShapeBinder] ShapeBinder
  Support = -> [Pad024]
  TraceSupport = false
FEATURE [Sketcher::SketchObject] Sketch027
  ExternalGeometry = -> [ShapeBinder]
  FullyConstrained = true
  MapMode = 5
  Support = -> [XY_Plane164]
  sketch-geometry (10):
    g0: LineSegment StartX=121.92 StartY=6.56 StartZ=0 EndX=-121.92 EndY=6.56 EndZ=0
    g1: LineSegment StartX=-121.92 StartY=6.56 StartZ=0 EndX=-121.92 EndY=34.56 EndZ=0
    g2: ArcOfCircle CenterX=-109.22 CenterY=34.56 CenterZ=0 NormalX=0 NormalY=0 NormalZ=1 AngleXU=0 Radius=12.7 StartAngle=1.5708 EndAngle=3.14159
    g3: LineSegment StartX=-109.22 StartY=47.26 StartZ=0 EndX=109.22 EndY=47.26 EndZ=0
    g4: ArcOfCircle CenterX=109.22 CenterY=34.56 CenterZ=0 NormalX=0 NormalY=0 NormalZ=1 AngleXU=0 Radius=12.7 StartAngle=0 EndAngle=1.5708
    g5: LineSegment StartX=121.92 StartY=34.56 StartZ=0 EndX=121.92 EndY=6.56 EndZ=0
    g6: Circle CenterX=-109.22 CenterY=34.56 CenterZ=0 NormalX=0 NormalY=0 NormalZ=1 AngleXU=0 Radius=1.55
    g7: Circle CenterX=-109.22 CenterY=34.56 CenterZ=0 NormalX=0 NormalY=0 NormalZ=1 AngleXU=0 Radius=1.55
    g8: Circle CenterX=109.22 CenterY=34.56 CenterZ=0 NormalX=0 NormalY=0 NormalZ=1 AngleXU=0 Radius=1.55
    g9: Circle CenterX=109.22 CenterY=34.56 CenterZ=0 NormalX=0 NormalY=0 NormalZ=1 AngleXU=0 Radius=1.55
  constraints (21):
    c: Coincident(g0,g1)
    c: Vertical(g1)
    c: Tangent(g1,g2) = 1.5708
    c: Horizontal(g3)
    c: Tangent(g3,g4) = 1.5708
    c: Coincident(g5,g0)
    c: Vertical(g5)
    c: Tangent(g4,g5) = 1.5708
    c: Tangent(g2,g3) = 1.5708
    c: Equal(g2,g4)
    c: Symmetric(g0,g0,g-2)
    c: Coincident(g0,g-4)
    c: Coincident(g2,g-3)
    c: Radius(g9) = 1.55
    c: Equal(g9,g8)
    c: Equal(g9,g6)
    c: Equal(g9,g7)
    c: Coincident(g7,g2)
    c: Coincident(g4,g8)
    c: Coincident(g6,g-5)
    c: Symmetric(g6,g9,g-2)
FEATURE [PartDesign::Pad] Pad026
  Direction = (1,1,1)
  Length = 3
  Length2 = 100
  Profile = -> Sketch027
  Type = 0
FEATURE [PartDesign::Body] Body016  label="ACR_top_back"
  Group = -> [Sketch027,ShapeBinder,Pad026]
  Origin = -> Origin163
  Placement = pos=(0,0,20) rot=(0,0,1;0rad)
  Tip = -> Pad026
FEATURE [Part::Part2DObjectPython] Shape2DView  label="ACR_bottom_2D"  # Draft 2D object (typed FeaturePython)
  AutoUpdate = true
  Base = -> Pad
  Clip = false
  FuseArch = false
  HiddenLines = false
  InPlace = true
  OnlySolids = false
  Projection = (0,0,1)
  ProjectionMode = 0
  SegmentLength = 0.05
  Tessellation = false
  VisibleOnly = false
FEATURE [Part::Part2DObjectPython] Shape2DView001  label="ACR_wall_front_2D"  # Draft 2D object (typed FeaturePython)
  AutoUpdate = true
  Base = -> Pad006
  Clip = false
  FuseArch = false
  HiddenLines = false
  InPlace = true
  OnlySolids = false
  Projection = (0,-1,0)
  ProjectionMode = 0
  SegmentLength = 0.05
  Tessellation = false
  VisibleOnly = false
FEATURE [Part::Part2DObjectPython] Shape2DView002  label="ACR_wall_back_2D"  # Draft 2D object (typed FeaturePython)
  AutoUpdate = true
  Base = -> Pocket001
  Clip = false
  FuseArch = false
  HiddenLines = false
  InPlace = true
  OnlySolids = false
  Projection = (0,-1,0)
  ProjectionMode = 0
  SegmentLength = 0.05
  Tessellation = false
  VisibleOnly = false
FEATURE [Part::Part2DObjectPython] Shape2DView003  label="ACR_top_front_2D"  # Draft 2D object (typed FeaturePython)
  AutoUpdate = true
  Clip = false
  FuseArch = false
  HiddenLines = false
  InPlace = true
  OnlySolids = false
  Projection = (0,0,1)
  ProjectionMode = 0
  SegmentLength = 0.05
  Tessellation = false
  VisibleOnly = false
FEATURE [Part::Part2DObjectPython] Shape2DView004  label="ACR_top_back_2D"  # Draft 2D object (typed FeaturePython)
  AutoUpdate = true
  Base = -> Pad026
  Clip = false
  FuseArch = false
  HiddenLines = false
  InPlace = true
  OnlySolids = false
  Projection = (0,0,1)
  ProjectionMode = 0
  SegmentLength = 0.05
  Tessellation = false
  VisibleOnly = false
FEATURE [Sketcher::SketchObject] Sketch028
  ExternalGeometry = -> [Pad021]
  FullyConstrained = true
  MapMode = 5
  Placement = pos=(0,0,20) rot=(0,0,1;0rad)
  Support = -> [Pad021]
  sketch-geometry (7):
    g0: LineSegment StartX=-106.47 StartY=-37.1477 StartZ=0 EndX=-106.47 EndY=-33.9723 EndZ=0
    g1: LineSegment StartX=-106.47 StartY=-33.9723 StartZ=0 EndX=-109.22 EndY=-32.3846 EndZ=0
    g2: LineSegment StartX=-109.22 StartY=-32.3846 StartZ=0 EndX=-111.97 EndY=-33.9723 EndZ=0
    g3: LineSegment StartX=-111.97 StartY=-33.9723 StartZ=0 EndX=-111.97 EndY=-37.1477 EndZ=0
    g4: LineSegment StartX=-111.97 StartY=-37.1477 StartZ=0 EndX=-109.22 EndY=-38.7354 EndZ=0
    g5: LineSegment StartX=-109.22 StartY=-38.7354 StartZ=0 EndX=-106.47 EndY=-37.1477 EndZ=0
    g6: Circle CenterX=-109.22 CenterY=-35.56 CenterZ=0 NormalX=0 NormalY=0 NormalZ=1 AngleXU=0 Radius=3.17543
  constraints (16):
    c: Coincident(g0,g1)
    c: Coincident(g1,g2)
    c: Coincident(g2,g3)
    c: Coincident(g3,g4)
    c: Coincident(g4,g5)
    c: Coincident(g5,g0)
    c: Equal(g0, g1-g5) x5
    c: PointOnObject(g0,g6)
    c: PointOnObject(g1,g6)
    c: PointOnObject(g2,g6)
    c: PointOnObject(g3,g6)
    c: PointOnObject(g4,g6)
    c: PointOnObject(g5,g6)
    c: Vertical(g0)
    c: DistanceX(g3,g0) = 5.5
    c: Coincident(g6,g-3)
FEATURE [PartDesign::Pocket] Pocket002
  BaseFeature = -> Pad021
  Direction = (1,1,1)
  Length = 20
  Length2 = 100
  Profile = -> Sketch028
  Type = 0
FEATURE [Sketcher::SketchObject] Sketch029
  ExternalGeometry = -> [Pad024]
  FullyConstrained = true
  MapMode = 5
  Placement = pos=(0,0,20) rot=(0,0,1;0rad)
  Support = -> [Pad024]
  sketch-geometry (14):
    g0: LineSegment StartX=-106.47 StartY=32.9723 StartZ=0 EndX=-106.47 EndY=36.1477 EndZ=0
    g1: LineSegment StartX=-106.47 StartY=36.1477 StartZ=0 EndX=-109.22 EndY=37.7354 EndZ=0
    g2: LineSegment StartX=-109.22 StartY=37.7354 StartZ=0 EndX=-111.97 EndY=36.1477 EndZ=0
    g3: LineSegment StartX=-111.97 StartY=36.1477 StartZ=0 EndX=-111.97 EndY=32.9723 EndZ=0
    g4: LineSegment StartX=-111.97 StartY=32.9723 StartZ=0 EndX=-109.22 EndY=31.3846 EndZ=0
    g5: LineSegment StartX=-109.22 StartY=31.3846 StartZ=0 EndX=-106.47 EndY=32.9723 EndZ=0
    g6: Circle CenterX=-109.22 CenterY=34.56 CenterZ=0 NormalX=0 NormalY=0 NormalZ=1 AngleXU=0 Radius=3.17543
    g7: LineSegment StartX=-106.47 StartY=16.8723 StartZ=0 EndX=-106.47 EndY=20.0477 EndZ=0
    g8: LineSegment StartX=-106.47 StartY=20.0477 StartZ=0 EndX=-109.22 EndY=21.6354 EndZ=0
    g9: LineSegment StartX=-109.22 StartY=21.6354 StartZ=0 EndX=-111.97 EndY=20.0477 EndZ=0
    g10: LineSegment StartX=-111.97 StartY=20.0477 StartZ=0 EndX=-111.97 EndY=16.8723 EndZ=0
    g11: LineSegment StartX=-111.97 StartY=16.8723 StartZ=0 EndX=-109.22 EndY=15.2846 EndZ=0
    g12: LineSegment StartX=-109.22 StartY=15.2846 StartZ=0 EndX=-106.47 EndY=16.8723 EndZ=0
    g13: Circle CenterX=-109.22 CenterY=18.46 CenterZ=0 NormalX=0 NormalY=0 NormalZ=1 AngleXU=0 Radius=3.17543
  constraints (32):
    c: Coincident(g0,g1)
    c: Coincident(g1,g2)
    c: Coincident(g2,g3)
    c: Coincident(g3,g4)
    c: Coincident(g4,g5)
    c: Coincident(g5,g0)
    c: Equal(g0, g1-g5) x5
    c: PointOnObject(g0,g6)
    c: PointOnObject(g1,g6)
    c: PointOnObject(g2,g6)
    c: PointOnObject(g3,g6)
    c: PointOnObject(g4,g6)
    c: PointOnObject(g5,g6)
    c: Coincident(g7,g8)
    c: Coincident(g8,g9)
    c: Coincident(g9,g10)
    c: Coincident(g10,g11)
    c: Coincident(g11,g12)
    c: Coincident(g12,g7)
    c: Equal(g7, g8-g12) x5
    c: PointOnObject(g7,g13)
    c: PointOnObject(g8,g13)
    c: PointOnObject(g9,g13)
    c: PointOnObject(g10,g13)
    c: PointOnObject(g11,g13)
    c: PointOnObject(g12,g13)
    c: Vertical(g7)
    c: Vertical(g0)
    c: DistanceX(g3,g0) = 5.5
    c: Equal(g3,g10)
    c: Coincident(g6,g-3)
    c: Coincident(g13,g-4)
FEATURE [PartDesign::Pocket] Pocket003
  BaseFeature = -> Pad024
  Direction = (1,1,1)
  Length = 20
  Length2 = 100
  Profile = -> Sketch029
  Type = 0
FEATURE [Sketcher::SketchObject] Sketch031
  ExternalGeometry = -> [Pocket002]
  FullyConstrained = true
  MapMode = 5
  Placement = pos=(0,0,20) rot=(0,0,1;0rad)
  Support = -> [Pocket002]
  sketch-geometry (4):
    g0: LineSegment StartX=-121.92 StartY=-25.4 StartZ=0 EndX=-109.17 EndY=-25.4 EndZ=0
    g1: LineSegment StartX=-109.17 StartY=-25.4 StartZ=0 EndX=-106.17 EndY=-29.4 EndZ=0
    g2: LineSegment StartX=-106.17 StartY=-29.4 StartZ=0 EndX=-121.92 EndY=-29.4 EndZ=0
    g3: LineSegment StartX=-121.92 StartY=-29.4 StartZ=0 EndX=-121.92 EndY=-25.4 EndZ=0
  constraints (12):
    c: Coincident(g0,g1)
    c: Coincident(g1,g2)
    c: Coincident(g2,g3)
    c: Coincident(g3,g0)
    c: Horizontal(g0)
    c: Horizontal(g2)
    c: Vertical(g3)
    c: DistanceY(g3,g3) = 4
    c: DistanceX(g-3,g0) = 0
    c: DistanceX(g0,g-3) = 3
    c: PointOnObject(g0,g-3)
    c: DistanceX(g1,g-3) = 0
FEATURE [PartDesign::Pocket] Pocket004
  BaseFeature = -> Pocket002
  Direction = (1,1,1)
  Length = 5
  Length2 = 100
  Profile = -> Sketch031
  Type = 1
FEATURE [Sketcher::SketchObject] Sketch032
  ExternalGeometry = -> [Pocket004]
  FullyConstrained = true
  MapMode = 5
  Placement = pos=(0,0,20) rot=(0,0,1;0rad)
  Support = -> [Pocket004]
  sketch-geometry (12):
    g0: LineSegment StartX=-119.92 StartY=-29.4 StartZ=0 EndX=-119.92 EndY=-28.9 EndZ=0
    g1: LineSegment StartX=-121.92 StartY=-29.4 StartZ=0 EndX=-119.92 EndY=-29.4 EndZ=0
    g2: LineSegment StartX=-121.92 StartY=-27.9 StartZ=0 EndX=-121.92 EndY=-29.4 EndZ=0
    g3: ArcOfCircle CenterX=-115.47 CenterY=-31.3504 CenterZ=0 NormalX=0 NormalY=0 NormalZ=1 AngleXU=0 Radius=7.45042 StartAngle=0.831858 EndAngle=2.57719
    g4: LineSegment StartX=-115.47 StartY=-23.9 StartZ=0 EndX=-115.47 EndY=-25.4 EndZ=0
    g5: ArcOfCircle CenterX=-110.991 CenterY=-26.4345 CenterZ=0 NormalX=0 NormalY=0 NormalZ=1 AngleXU=0 Radius=0.8 StartAngle=3.92926 EndAngle=7.11504
    g6: ArcOfCircle CenterX=-115.174 CenterY=-30.6365 CenterZ=0 NormalX=0 NormalY=0 NormalZ=1 AngleXU=0 Radius=5.12905 StartAngle=0.787668 EndAngle=2.70753
    g7: ArcOfCircle CenterX=-118.92 CenterY=-28.9 CenterZ=0 NormalX=0 NormalY=0 NormalZ=1 AngleXU=0 Radius=1 StartAngle=2.70753 EndAngle=3.14159
    g8: ArcOfCircle CenterX=-120.92 CenterY=-27.9 CenterZ=0 NormalX=0 NormalY=0 NormalZ=1 AngleXU=0 Radius=1 StartAngle=2.57719 EndAngle=3.14159
    g9: LineSegment StartX=-121.92 StartY=-29.4 StartZ=0 EndX=-121.92 EndY=-30.4 EndZ=0
    g10: LineSegment StartX=-121.92 StartY=-30.4 StartZ=0 EndX=-119.92 EndY=-30.4 EndZ=0
    g11: LineSegment StartX=-119.92 StartY=-30.4 StartZ=0 EndX=-119.92 EndY=-29.4 EndZ=0
  constraints (34):
    c: Coincident(g1,g0)
    c: Horizontal(g1)
    c: Coincident(g2,g1)
    c: Vertical(g2)
    c: Vertical(g0)
    c: Coincident(g1,g-4)
    c: DistanceX(g1,g1) = 2
    c: Vertical(g4)
    c: DistanceY(g4,g4) = 1.5
    c: DistanceY(g4,g-5) = 0
    c: PointOnObject(g4,g3)
    c: Tangent(g5,g3) = -1.5708
    c: Radius(g5) = 0.8
    c: Perpendicular(g3,g4)
    c: Tangent(g0,g7) = 1.5708
    c: Tangent(g3,g8) = -1.5708
    c: Tangent(g2,g8) = -1.5708
    c: Radius(g8) = 1
    c: Radius(g7) = 1
    c: DistanceY(g0,g0) = 0.5
    c: DistanceY(g2,g2) = 1.5
    c: DistanceX(g4,g-5) = 6.3
    c: Angle(g3) = 1.74533
    c: Coincident(g1,g9)
    c: Vertical(g9)
    c: Coincident(g9,g10)
    c: Horizontal(g10)
    c: Coincident(g10,g11)
    c: Coincident(g11,g0)
    c: Vertical(g11)
    c: DistanceY(g9,g9) = 1
    c: Tangent(g6,g5) = 1.5708
    c: Tangent(g6,g7) = -1.5708
    c: Angle(g6) = 1.91986
FEATURE [PartDesign::Pad] Pad029
  BaseFeature = -> Pocket004
  Direction = (1,1,1)
  Length = 16.4
  Length2 = 100
  Profile = -> Sketch032
  Refine = true
  Reversed = true
  Type = 0
FEATURE [PartDesign::SubShapeBinder] Binder
  BindCopyOnChange = 0
  BindMode = 0
  ClaimChildren = false
  Context = -> Body015 [Binder.]
  Fuse = false
  MakeFace = true
  OffsetFill = false
  OffsetIntersection = false
  OffsetJoinType = 0
  OffsetOpenResult = false
  PartialLoad = false
  Refine = true
  Relative = true
  Support = -> [Body012[Pad029.Face29]]
  _Version = 2
FEATURE [Sketcher::SketchObject] Sketch026
  ExternalGeometry = -> [Binder]
  FullyConstrained = true
  MapMode = 5
  Support = -> [XY_Plane163]
  sketch-geometry (8):
    g0: LineSegment StartX=-121.92 StartY=-6.4 StartZ=0 EndX=121.92 EndY=-6.4 EndZ=0
    g1: LineSegment StartX=121.92 StartY=-6.4 StartZ=0 EndX=121.92 EndY=-16.56 EndZ=0
    g2: ArcOfCircle CenterX=109.22 CenterY=-16.56 CenterZ=0 NormalX=0 NormalY=0 NormalZ=1 AngleXU=0 Radius=12.7 StartAngle=4.71239 EndAngle=6.28319
    g3: LineSegment StartX=109.22 StartY=-29.26 StartZ=0 EndX=-109.22 EndY=-29.26 EndZ=0
    g4: ArcOfCircle CenterX=-109.22 CenterY=-16.56 CenterZ=0 NormalX=0 NormalY=0 NormalZ=1 AngleXU=0 Radius=12.7 StartAngle=3.14159 EndAngle=4.71239
    g5: LineSegment StartX=-121.92 StartY=-16.56 StartZ=0 EndX=-121.92 EndY=-6.4 EndZ=0
    g6: Circle CenterX=-109.22 CenterY=-16.56 CenterZ=0 NormalX=0 NormalY=0 NormalZ=1 AngleXU=0 Radius=1.55
    g7: Circle CenterX=109.22 CenterY=-16.56 CenterZ=0 NormalX=0 NormalY=0 NormalZ=1 AngleXU=0 Radius=1.55
  constraints (18):
    c: Coincident(g0,g1)
    c: Tangent(g1,g2) = 1.5708
    c: Horizontal(g3)
    c: Tangent(g3,g4) = 1.5708
    c: Coincident(g5,g0)
    c: Vertical(g5)
    c: Vertical(g1)
    c: Equal(g2,g4)
    c: Tangent(g2,g3) = 1.5708
    c: Tangent(g4,g5) = 1.5708
    c: Symmetric(g0,g0,g-2)
    c: Radius(g6) = 1.55
    c: Coincident(g6,g4)
    c: Coincident(g7,g2)
    c: Equal(g7,g6)
    c: Coincident(g4,g-5)
    c: Equal(g-5,g4)
    c: PointOnObject(g-4,g0)
FEATURE [PartDesign::Pad] Pad027
  Direction = (1,1,1)
  Length = 3
  Length2 = 100
  Profile = -> Sketch026
  Type = 0
FEATURE [PartDesign::Body] Body015  label="ACR_top_front"
  Group = -> [Sketch026,Pad027,Binder]
  Origin = -> Origin162
  Placement = pos=(0,0,20) rot=(0,0,1;0rad)
  Tip = -> Pad027
FEATURE [PartDesign::Plane] DatumPlane001
  Length = 60
  MapMode = 5
  Placement = pos=(-121.92,0,0) rot=(0.57735,-0.57735,-0.57735;2.0944rad)
  ResizeMode = 0
  Width = 60
FEATURE [Sketcher::SketchObject] Sketch034
  ExternalGeometry = -> [Pad029]
  FullyConstrained = true
  Placement = pos=(-121.92,0,0) rot=(0.57735,-0.57735,-0.57735;2.0944rad)
  Support = -> [DatumPlane001]
  sketch-geometry (5):
    g0: LineSegment StartX=26.9 StartY=20 StartZ=0 EndX=26.9 EndY=21 EndZ=0
    g1: LineSegment StartX=26.9 StartY=21 StartZ=0 EndX=22.9 EndY=21 EndZ=0
    g2: LineSegment StartX=22.9 StartY=21 StartZ=0 EndX=22.9 EndY=17 EndZ=0
    g3: LineSegment StartX=22.9 StartY=17 StartZ=0 EndX=23.9 EndY=17 EndZ=0
    g4: ArcOfCircle CenterX=26.9 CenterY=17 CenterZ=0 NormalX=0 NormalY=0 NormalZ=1 AngleXU=0 Radius=3 StartAngle=1.5708 EndAngle=3.14159
  constraints (15):
    c: Coincident(g0,g1)
    c: Horizontal(g1)
    c: Coincident(g1,g2)
    c: Vertical(g2)
    c: Coincident(g2,g3)
    c: Horizontal(g3)
    c: Perpendicular(g3,g4) = 4.71239
    c: Coincident(g4,g0)
    c: Vertical(g0)
    c: Equal(g3,g0)
    c: Equal(g1,g2)
    c: Radius(g4) = 3
    c: DistanceX(g3,g3) = 1
    c: PointOnObject(g0,g-3)
    c: Vertical(g3,g-3)
FEATURE [Sketcher::SketchObject] Sketch035
  ExternalGeometry = -> [Pad002]
  FullyConstrained = true
  MapMode = 5
  Placement = pos=(0,6,0) rot=(0,0.707107,0.707107;3.14159rad)
  Support = -> [Pad002]
  sketch-geometry (1):
    g0: Circle CenterX=114.3 CenterY=6.4 CenterZ=0 NormalX=0 NormalY=0 NormalZ=1 AngleXU=0 Radius=1.1
  constraints (3):
    c: Radius(g0) = 1.1
    c: Distance(g0,g-3) = 12.7
    c: DistanceY(g-3,g0) = 4.8
FEATURE [PartDesign::Pocket] Pocket006
  BaseFeature = -> Pad002
  Direction = (1,1,1)
  Length = 5
  Length2 = 100
  Profile = -> Sketch035
  Type = 1
FEATURE [PartDesign::Mirrored] Mirrored
  BaseFeature = -> Pocket006
  MirrorPlane = -> Sketch035 [V_Axis]
  Originals = -> [Pocket006]
FEATURE [PartDesign::Body] Body002  label="ACR_front"
  Group = -> [Sketch002,Pad002,Sketch035,Pocket006,Mirrored]
  Origin = -> Origin002
  Placement = pos=(0,-6,1.6) rot=(0,0,1;0rad)
  Tip = -> Mirrored
FEATURE [Part::Part2DObjectPython] Shape2DView005  # Draft 2D object (typed FeaturePython)
  AutoUpdate = true
  Base = -> Body002
  Clip = false
  FuseArch = false
  HiddenLines = false
  InPlace = true
  OnlySolids = false
  Projection = (0,-1,0)
  ProjectionMode = 0
  SegmentLength = 0.05
  Tessellation = false
  VisibleOnly = false
FEATURE [Sketcher::SketchObject] Sketch038
  FullyConstrained = false
  sketch-geometry (12):
    g0: LineSegment StartX=-3.2 StartY=-127 StartZ=0 EndX=-257.2 EndY=-127 EndZ=0
    g1: LineSegment StartX=-3.2 StartY=127 StartZ=0 EndX=-3.2 EndY=-127 EndZ=0
    g2: LineSegment StartX=-257.2 StartY=127 StartZ=0 EndX=-257.2 EndY=-127 EndZ=0
    g3: LineSegment StartX=-3.2 StartY=127 StartZ=0 EndX=-257.2 EndY=127 EndZ=0
    g4: ArcOfCircle CenterX=-16 CenterY=-114.3 CenterZ=0 NormalX=0 NormalY=0 NormalZ=1 AngleXU=-1.5708 Radius=1 StartAngle=3.14159 EndAngle=6.28319
    g5: LineSegment StartX=-6.9 StartY=-115.3 StartZ=0 EndX=-16 EndY=-115.3 EndZ=0
    g6: LineSegment StartX=-6.9 StartY=-113.3 StartZ=0 EndX=-16 EndY=-113.3 EndZ=0
    g7: ArcOfCircle CenterX=-6.9 CenterY=-114.3 CenterZ=0 NormalX=0 NormalY=0 NormalZ=1 AngleXU=-1.5708 Radius=1 StartAngle=9e-16 EndAngle=3.14159
    g8: LineSegment StartX=-6.9 StartY=115.3 StartZ=0 EndX=-16 EndY=115.3 EndZ=0
    g9: ArcOfCircle CenterX=-6.9 CenterY=114.3 CenterZ=0 NormalX=0 NormalY=0 NormalZ=1 AngleXU=1.5708 Radius=1 StartAngle=3.14159 EndAngle=6.28319
    g10: LineSegment StartX=-6.9 StartY=113.3 StartZ=0 EndX=-16 EndY=113.3 EndZ=0
    g11: ArcOfCircle CenterX=-16 CenterY=114.3 CenterZ=0 NormalX=0 NormalY=0 NormalZ=1 AngleXU=1.5708 Radius=1 StartAngle=0 EndAngle=3.14159
FEATURE [PartDesign::SubShapeBinder] Binder001
  BindCopyOnChange = 0
  BindMode = 0
  ClaimChildren = false
  Context = -> Body014 [Binder001.]
  Fuse = false
  MakeFace = true
  OffsetFill = false
  OffsetIntersection = false
  OffsetJoinType = 0
  OffsetOpenResult = false
  PartialLoad = false
  Refine = true
  Relative = true
  Support = -> [Body012[Pocket008.Face37]]
  _Version = 2
FEATURE [Sketcher::SketchObject] Sketch039
  ExternalGeometry = -> [Pocket003]
  FullyConstrained = false
  MapMode = 5
  Placement = pos=(0,0,0) rot=(1,0,0;3.14159rad)
  Support = -> [Pocket003]
  sketch-geometry (6):
    g0: LineSegment StartX=-121.92 StartY=-10.56 StartZ=0 EndX=-106.17 EndY=-10.56 EndZ=0
    g1: LineSegment StartX=-106.17 StartY=-10.56 StartZ=0 EndX=-109.17 EndY=-6.56 EndZ=0
    g2: LineSegment StartX=-109.17 StartY=-6.56 StartZ=0 EndX=-121.92 EndY=-6.56 EndZ=0
    g3: LineSegment StartX=-121.92 StartY=-6.56 StartZ=0 EndX=-121.92 EndY=-10.56 EndZ=0
    g4: LineSegment StartX=-109.17 StartY=6.4 StartZ=0 EndX=-121.92 EndY=6.4 EndZ=0
    g5: LineSegment StartX=-121.92 StartY=10.4 StartZ=0 EndX=-121.92 EndY=6.4 EndZ=0
  constraints (11):
    c: Horizontal(g0)
    c: Coincident(g0,g1)
    c: Coincident(g1,g2)
    c: Horizontal(g2)
    c: Coincident(g2,g3)
    c: Coincident(g3,g0)
    c: Vertical(g3)
    c: Horizontal(g4)
    c: Coincident(g5,g4)
    c: Equal(g4,g2)
    c: Equal(g5,g3)
FEATURE [PartDesign::Pocket] Pocket009
  BaseFeature = -> Pocket003
  Direction = (1,1,1)
  Length = 5
  Length2 = 100
  Profile = -> Sketch039
  Type = 1
FEATURE [PartDesign::SubShapeBinder] Binder002
  BindCopyOnChange = 0
  BindMode = 0
  ClaimChildren = false
  Context = -> Body014 [Binder002.]
  Fuse = false
  MakeFace = true
  OffsetFill = false
  OffsetIntersection = false
  OffsetJoinType = 0
  OffsetOpenResult = false
  PartialLoad = false
  Refine = true
  Relative = true
  Support = -> [Body012[Pad029.Face29]]
  _Version = 2
FEATURE [Sketcher::SketchObject] Sketch040
  ExternalGeometry = -> [Binder002,Pocket009]
  FullyConstrained = true
  MapMode = 5
  Placement = pos=(0,0,20) rot=(0,0,1;0rad)
  Support = -> [Pocket009]
  sketch-geometry (12):
    g0: LineSegment StartX=-121.92 StartY=10.56 StartZ=0 EndX=-121.92 EndY=9.06 EndZ=0
    g1: ArcOfCircle CenterX=-120.92 CenterY=9.06 CenterZ=0 NormalX=0 NormalY=0 NormalZ=1 AngleXU=0 Radius=1 StartAngle=3.14159 EndAngle=3.706
    g2: ArcOfCircle CenterX=-115.47 CenterY=12.5104 CenterZ=0 NormalX=0 NormalY=0 NormalZ=1 AngleXU=0 Radius=7.45042 StartAngle=3.706 EndAngle=5.45133
    g3: ArcOfCircle CenterX=-110.991 CenterY=7.59454 CenterZ=0 NormalX=0 NormalY=0 NormalZ=1 AngleXU=0 Radius=0.8 StartAngle=5.45133 EndAngle=8.63711
    g4: ArcOfCircle CenterX=-115.174 CenterY=11.7965 CenterZ=0 NormalX=0 NormalY=0 NormalZ=1 AngleXU=0 Radius=5.12905 StartAngle=3.57565 EndAngle=5.49552
    g5: ArcOfCircle CenterX=-118.92 CenterY=10.06 CenterZ=0 NormalX=0 NormalY=0 NormalZ=1 AngleXU=0 Radius=1 StartAngle=3.14159 EndAngle=3.57565
    g6: LineSegment StartX=-119.92 StartY=10.06 StartZ=0 EndX=-119.92 EndY=10.56 EndZ=0
    g7: LineSegment StartX=-119.92 StartY=10.56 StartZ=0 EndX=-121.92 EndY=10.56 EndZ=0
    g8: LineSegment StartX=-119.92 StartY=-10.4 StartZ=0 EndX=-121.92 EndY=-10.4 EndZ=0
    g9: LineSegment StartX=-121.92 StartY=-10.4 StartZ=0 EndX=-121.92 EndY=-8.9 EndZ=0
    g10: LineSegment StartX=-110.991 StartY=-7.43454 StartZ=0 EndX=-110.991 EndY=-10.4 EndZ=0
    g11: LineSegment StartX=-110.991 StartY=7.59454 StartZ=0 EndX=-110.991 EndY=10.56 EndZ=0
  constraints (35):
    c: Vertical(g0)
    c: Tangent(g0,g1) = -1.5708
    c: Tangent(g1,g2) = -1.5708
    c: Tangent(g2,g3) = -1.5708
    c: Tangent(g3,g4) = 1.5708
    c: Tangent(g4,g5) = -1.5708
    c: Coincident(g6,g7)
    c: Coincident(g7,g0)
    c: Horizontal(g7)
    c: Equal(g-7,g6)
    c: Vertical(g6)
    c: Equal(g4,g-5)
    c: Equal(g3,g-4)
    c: Equal(g2,g-3)
    c: Equal(g1,g-8)
    c: Coincident(g8,g-7)
    c: PointOnObject(g8,g-9)
    c: Horizontal(g8)
    c: Equal(g8,g7)
    c: Angle(g-5) = 1.91986
    c: Angle(g-3) = 1.74533
    c: Tangent(g5,g6) = 1.5708
    c: Coincident(g9,g8)
    c: Coincident(g9,g-9)
    c: Equal(g9,g0)
    c: Coincident(g0,g-10)
    c: Coincident(g10,g-4)
    c: PointOnObject(g10,g-11)
    c: Vertical(g10)
    c: Coincident(g11,g3)
    c: PointOnObject(g11,g-10)
    c: Vertical(g11)
    c: Equal(g11,g10)
    c: Angle(g2) = 1.74533
    c: Angle(g4) = 1.91986
FEATURE [PartDesign::Pad] Pad031
  BaseFeature = -> Pocket009
  Direction = (1,1,1)
  Length = 16.4
  Length2 = 100
  Profile = -> Sketch040
  Refine = true
  Reversed = true
  Type = 0
FEATURE [PartDesign::SubShapeBinder] Binder003
  BindCopyOnChange = 0
  BindMode = 0
  ClaimChildren = false
  Context = -> Body014 [Binder003.]
  Fuse = false
  MakeFace = true
  OffsetFill = false
  OffsetIntersection = false
  OffsetJoinType = 0
  OffsetOpenResult = false
  PartialLoad = false
  Refine = true
  Relative = true
  Support = -> [Body012[Pad030.]]
  _Version = 2
FEATURE [PartDesign::Plane] CopyDatumPlane
  Length = 84.2589
  Placement = pos=(-114.3,0,0) rot=(0.57735,-0.57735,-0.57735;2.0944rad)
  ResizeMode = 0
  Width = 62.0199
FEATURE [PartDesign::SubShapeBinder] Binder004
  BindCopyOnChange = 0
  BindMode = 0
  ClaimChildren = false
  Context = -> Body014 [Binder004.]
  Fuse = false
  MakeFace = true
  OffsetFill = false
  OffsetIntersection = false
  OffsetJoinType = 0
  OffsetOpenResult = false
  PartialLoad = false
  Refine = true
  Relative = true
  Support = -> [Body012[Pocket005.Sketch034.]]
  _Version = 2
FEATURE [PartDesign::Plane] CopyDatumPlane001
  Length = 84.2589
  Placement = pos=(-121.92,0,0) rot=(0.57735,-0.57735,-0.57735;2.0944rad)
  ResizeMode = 0
  Width = 62.0199
FEATURE [Sketcher::SketchObject] Sketch042
  ExternalGeometry = -> [Binder004,Pad031]
  FullyConstrained = true
  MapMode = 5
  Placement = pos=(-121.92,0,0) rot=(0.57735,-0.57735,-0.57735;2.0944rad)
  Support = -> [CopyDatumPlane001]
  sketch-geometry (5):
    g0: LineSegment StartX=-5.06 StartY=17 StartZ=0 EndX=-4.06 EndY=17 EndZ=0
    g1: LineSegment StartX=-4.06 StartY=17 StartZ=0 EndX=-4.06 EndY=21 EndZ=0
    g2: LineSegment StartX=-4.06 StartY=21 StartZ=0 EndX=-8.06 EndY=21 EndZ=0
    g3: LineSegment StartX=-8.06 StartY=21 StartZ=0 EndX=-8.06 EndY=20 EndZ=0
    g4: ArcOfCircle CenterX=-8.06 CenterY=17 CenterZ=0 NormalX=0 NormalY=0 NormalZ=1 AngleXU=0 Radius=3 StartAngle=8.2866e-12 EndAngle=1.5708
  constraints (16):
    c: Coincident(g3,g4)
    c: Coincident(g2,g3)
    c: Coincident(g0,g4)
    c: Coincident(g0,g1)
    c: Horizontal(g2)
    c: Vertical(g1)
    c: Horizontal(g0)
    c: Vertical(g3)
    c: Equal(g2,g1)
    c: Equal(g3,g0)
    c: Equal(g2,g-3)
    c: Equal(g3,g-4)
    c: Equal(g4,g-5)
    c: PointOnObject(g3,g-6)
    c: Coincident(g1,g2)
    c: Vertical(g-6,g0)
FEATURE [PartDesign::SubShapeBinder] Binder005
  BindCopyOnChange = 0
  BindMode = 0
  ClaimChildren = false
  Context = -> Body014 [Binder005.]
  Fuse = false
  MakeFace = true
  OffsetFill = false
  OffsetIntersection = false
  OffsetJoinType = 0
  OffsetOpenResult = false
  PartialLoad = false
  Refine = true
  Relative = true
  Support = -> [Body012[Pocket007.Sketch036.]]
  _Version = 2
FEATURE [PartDesign::SubShapeBinder] Binder006
  BindCopyOnChange = 0
  BindMode = 0
  ClaimChildren = false
  Context = -> Body014 [Binder006.]
  Fuse = false
  MakeFace = true
  OffsetFill = false
  OffsetIntersection = false
  OffsetJoinType = 0
  OffsetOpenResult = false
  PartialLoad = false
  Refine = true
  Relative = true
  Support = -> [Body012[Pocket008.Sketch037.]]
  _Version = 2
FEATURE [PartDesign::Pocket] Pocket013
  BaseFeature = -> Pad029
  Direction = (1,1,1)
  Length = 5
  Length2 = 100
  Profile = -> Sketch034
  Type = 1
FEATURE [Sketcher::SketchObject] Sketch036
  AttachmentOffset = pos=(0,0,-5) rot=(0,0,1;0rad)
  ExternalGeometry = -> [Pocket013]
  FullyConstrained = true
  MapMode = 5
  Placement = pos=(0,-34.4,1.1e-15) rot=(0,0.707107,0.707107;3.14159rad)
  Support = -> [Pocket013]
  sketch-geometry (1):
    g0: Circle CenterX=114.3 CenterY=8 CenterZ=0 NormalX=0 NormalY=0 NormalZ=1 AngleXU=0 Radius=2.1
  constraints (3):
    c: Radius(g0) = 2.1
    c: Distance(g0,g-4) = 12
    c: DistanceX(g0,g-5) = 7.62
FEATURE [PartDesign::Pocket] Pocket014
  BaseFeature = -> Pocket013
  Direction = (1,1,1)
  Length = 5
  Length2 = 100
  Profile = -> Sketch036
  Type = 1
FEATURE [Sketcher::SketchObject] Sketch037
  ExternalGeometry = -> [Pocket014]
  FullyConstrained = true
  MapMode = 5
  Placement = pos=(0,-29.4,0) rot=(0,0.707107,0.707107;3.14159rad)
  Support = -> [Pocket014]
  sketch-geometry (1):
    g0: Circle CenterX=114.3 CenterY=8 CenterZ=0 NormalX=0 NormalY=0 NormalZ=1 AngleXU=0 Radius=2.1
  constraints (2):
    c: Radius(g0) = 2.1
    c: Coincident(g0,g-4)
FEATURE [PartDesign::Pocket] Pocket015
  BaseFeature = -> Pocket014
  Direction = (1,1,1)
  Length = 5
  Length2 = 100
  Profile = -> Sketch037
  Reversed = true
  Type = 1
FEATURE [Sketcher::SketchObject] Sketch045
  ExternalGeometry = -> [Pocket015]
  FullyConstrained = true
  MapMode = 5
  Placement = pos=(0,-29.4,0) rot=(0,0.707107,0.707107;3.14159rad)
  Support = -> [Pocket015]
  sketch-geometry (1):
    g0: Circle CenterX=114.3 CenterY=8 CenterZ=0 NormalX=0 NormalY=0 NormalZ=1 AngleXU=0 Radius=0.9
  constraints (2):
    c: Radius(g0) = 0.9
    c: Coincident(g0,g-3)
FEATURE [PartDesign::Pocket] Pocket016
  BaseFeature = -> Pocket015
  Direction = (1,1,1)
  Length = 5
  Length2 = 100
  Profile = -> Sketch045
  Type = 1
FEATURE [PartDesign::Body] Body012  label="Corner_front_left"
  Group = -> [Sketch016,Pad017,Sketch020,Pad021,Sketch028,Pocket002,Sketch031,Pocket004,Sketch032,Pad029,DatumPlane001,Sketch034,Sketch036,Sketch037,Pocket013,Pocket014,Pocket015,Sketch045,Pocket016]
  Placement = pos=(0,19,0) rot=(0,0,1;0rad)
  Tip = -> Pocket016
FEATURE [Part::Mirroring] mirror  label="Corner_front_right (mirrored)"
  Base = (9.53674e-07,-17.0771,10)
  Normal = (1,0,-1.19209e-07)
  Source = -> Body012
FEATURE [PartDesign::Pocket] Pocket017
  BaseFeature = -> Pad031
  Direction = (1,0,0)
  Length = 5
  Length2 = 100
  Profile = -> Sketch042
  Type = 1
FEATURE [Sketcher::SketchObject] Sketch043
  ExternalGeometry = -> [Pocket017]
  FullyConstrained = true
  MapMode = 5
  Placement = pos=(0,15.56,0) rot=(1,0,0;1.5708rad)
  sketch-geometry (1):
    g0: Circle CenterX=-114.3 CenterY=8 CenterZ=0 NormalX=0 NormalY=0 NormalZ=1 AngleXU=0 Radius=2.1
  constraints (3):
    c: Radius(g0) = 2.1
    c: Distance(g0,g-4) = 12
    c: Distance(g0,g-5) = 7.62
FEATURE [PartDesign::Pocket] Pocket018
  BaseFeature = -> Pocket017
  Direction = (0,1,-2e-16)
  Length = 5
  Length2 = 100
  Profile = -> Sketch043
  Type = 1
FEATURE [Sketcher::SketchObject] Sketch044
  ExternalGeometry = -> [Pocket018]
  FullyConstrained = true
  MapMode = 5
  Placement = pos=(0,10.56,0) rot=(1,0,0;1.5708rad)
  sketch-geometry (1):
    g0: Circle CenterX=-114.3 CenterY=8 CenterZ=0 NormalX=0 NormalY=0 NormalZ=1 AngleXU=0 Radius=2.1
  constraints (2):
    c: Equal(g0,g-4)
    c: Coincident(g0,g-4)
FEATURE [PartDesign::Pocket] Pocket019
  BaseFeature = -> Pocket018
  Direction = (0,1,-2e-16)
  Length = 5
  Length2 = 100
  Profile = -> Sketch044
  Reversed = true
  Type = 1
FEATURE [Sketcher::SketchObject] Sketch046
  ExternalGeometry = -> [Pocket019]
  FullyConstrained = false
  MapMode = 5
  Placement = pos=(0,42.164,0) rot=(0,0.707107,0.707107;3.14159rad)
  Support = -> [Pocket019]
  sketch-geometry (1):
    g0: Circle CenterX=-114.3 CenterY=8 CenterZ=0 NormalX=0 NormalY=0 NormalZ=1 AngleXU=0 Radius=0.9
  constraints (2):
    c: Radius(g0) = 0.9
    c: Coincident(g0,g-3)
FEATURE [PartDesign::Pocket] Pocket020
  BaseFeature = -> Pocket019
  Direction = (1,1,1)
  Length = 5
  Length2 = 100
  Profile = -> Sketch046
  Refine = true
  Type = 1
FEATURE [PartDesign::Body] Body014  label="Corner_back_left"
  Group = -> [Sketch024,Pad023,Sketch025,Pad024,Sketch029,Pocket003,Binder001,Sketch039,Pocket009,Binder002,Sketch040,Pad031,Binder003,CopyDatumPlane,Binder004,CopyDatumPlane001,Sketch042,Binder005,Sketch043,Binder006,Sketch044,Pocket017,Pocket018,Pocket019,Sketch046,Pocket020]
  Origin = -> Origin161
  Tip = -> Pocket020
FEATURE [Part::Mirroring] mirror001  label="Corner_back_right (mirrored)"
  Base = (0,0,0)
  Normal = (1,0,0)
  Source = -> Body014
FEATURE [Part::FeaturePython] Screw  label="M2x12-Screw"  # Fasteners workbench fastener (typed FeaturePython)
  Placement = pos=(-114.3,-15.4,8) rot=(1,0,0;1.5708rad)
  diameter = 2
  invert = false
  leftHanded = false
  length = 6
  lengthCustom = 12
  matchOuter = false
  offset = 0
  thread = false
  type = 32
FEATURE [TechDraw::DrawSVGTemplate] Template
  Height = 297
  Orientation = 1
  Width = 420
FEATURE [TechDraw::DrawViewPart] View
  CoarseView = false
  Direction = (0,-1,0)
  Focus = 100
  HardHidden = false
  IsoCount = 0
  IsoHidden = false
  IsoVisible = false
  LockPosition = false
  Perspective = false
  Rotation = 0
  ScaleType = 0
  ScrubCount = 0
  SeamHidden = false
  SeamVisible = true
  SmoothHidden = false
  SmoothVisible = true
  Source = -> [Body002,Body014]
  X = 210
  XDirection = (1,0,0)
  Y = 148.5
FEATURE [TechDraw::DrawViewDimension] Dimension
  AngleOverride = false
  Arbitrary = false
  ArbitraryTolerances = false
  EqualTolerance = true
  ExtensionAngle = 0
  FormatSpec = %.2f
  FormatSpecOverTolerance = %+.2w
  FormatSpecUnderTolerance = %+.2w
  Inverted = false
  LineAngle = 0
  LockPosition = false
  MeasureType = 1
  OverTolerance = 0
  References2D = -> [View]
  Rotation = 0
  ScaleType = 0
  TheoreticalExact = false
  Type = 1
  UnderTolerance = 0
  X = 0.857833
  Y = -131.18
FEATURE [TechDraw::DrawViewDimension] Dimension003
  AngleOverride = false
  Arbitrary = false
  ArbitraryTolerances = false
  EqualTolerance = true
  ExtensionAngle = 0
  FormatSpec = %.2f
  FormatSpecOverTolerance = %+.2w
  FormatSpecUnderTolerance = %+.2w
  Inverted = false
  LineAngle = 0
  LockPosition = false
  MeasureType = 1
  OverTolerance = 0
  References2D = -> [View]
  Rotation = 0
  ScaleType = 0
  TheoreticalExact = false
  Type = 2
  UnderTolerance = 0
  X = -142.078
  Y = -102.897
FEATURE [TechDraw::DrawHatch] Hatch  label="HatchF1"
  HatchPattern = <path>
  Source = -> View [Face1]
FEATURE [TechDraw::DrawViewDimension] Dimension004
  AngleOverride = false
  Arbitrary = false
  ArbitraryTolerances = false
  EqualTolerance = true
  ExtensionAngle = 0
  FormatSpec = ⌀%.2f [2.2mm]
  FormatSpecOverTolerance = %+.2w
  FormatSpecUnderTolerance = %+.2w
  Inverted = false
  LineAngle = 0
  LockPosition = false
  MeasureType = 1
  OverTolerance = 0
  References2D = -> [View]
  Rotation = 0
  ScaleType = 0
  TheoreticalExact = false
  Type = 5
  UnderTolerance = 0
  X = 144.832
  Y = -106.574
FEATURE [TechDraw::DrawPage] Page
  KeepUpdated = true
  NextBalloonIndex = 1
  ProjectionType = 0
  Template = -> Template
  Views = -> [View,Dimension,Dimension003,Dimension004]
note: 1 file-system path scrubbed to <path> (originals preserved in the JSON sidecar)
